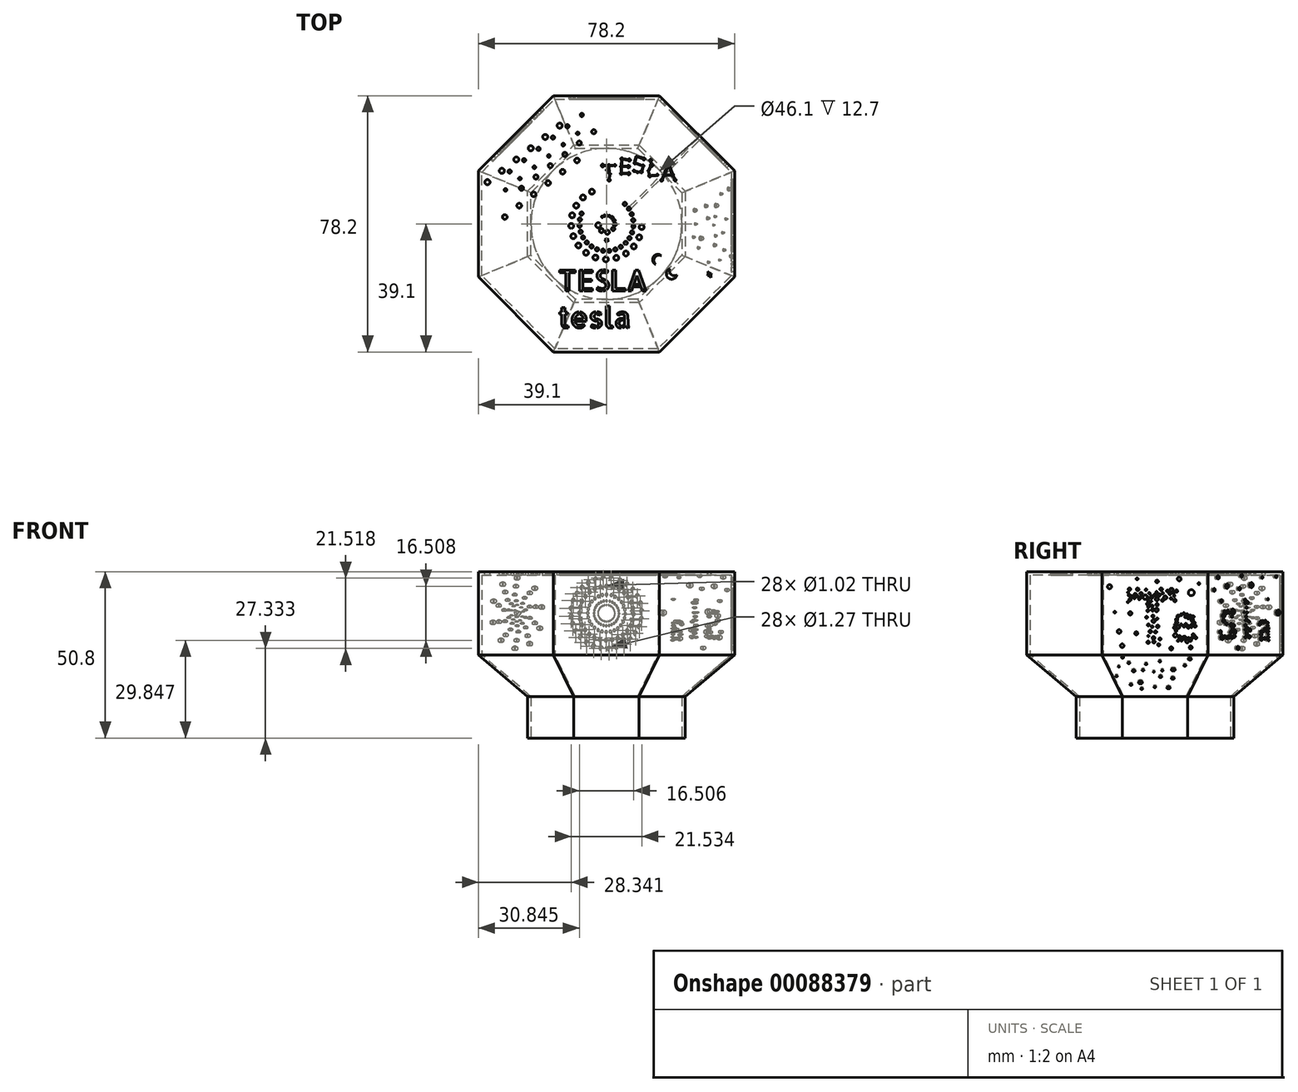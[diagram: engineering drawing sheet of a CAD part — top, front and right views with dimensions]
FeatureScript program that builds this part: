
annotation { "Feature Type Name" : "Feature", "Feature Type Description" : "" }
export const myFeature = defineFeature(function(context is Context, id is Id, definition is map)
    precondition{}
    {
        {
            var Q0;
            Q0=qCreatedBy(makeId("Top.planeOp"),FACE);
            cPlane(context, id + "F0", {"entities" : qUnion([Q0]), "cplaneType" : CPlaneType.OFFSET, "offset" : 12.7 * mm, "width" : 152.4 * mm, "height" : 152.4 * mm});
        }
        {
            var Q0;
            Q0=qCreatedBy(makeId("Top.planeOp"),FACE);
            cPlane(context, id + "F1", {"entities" : qUnion([Q0]), "cplaneType" : CPlaneType.OFFSET, "offset" : 25.4 * mm, "width" : 152.4 * mm, "height" : 152.4 * mm});
        }
        {
            var Q0;
            Q0=qCreatedBy(makeId("Top.planeOp"),FACE);
            cPlane(context, id + "F2", {"entities" : qUnion([Q0]), "cplaneType" : CPlaneType.OFFSET, "offset" : 50.8 * mm, "width" : 152.4 * mm, "height" : 152.4 * mm});
        }
        {
            var Q0;
            Q0=qCreatedBy(makeId("Top.planeOp"),FACE);
            var sketch = newSketch(context, id + "F3", { "sketchPlane" : qUnion([Q0])});
            skCircle(sketch, "E0", {"center": v(0, 0) * mm, "radius": 23.05 * mm});
            skCircle(sketch, "E1.cCircle", {"center": v(0, 0) * mm, "radius": 24.05 * mm, "construction": true});
            skLineSegment(sketch, "E1.0", {"start": v(-9.96, 24.05) * mm, "end": v(9.96, 24.05) * mm});
            skLineSegment(sketch, "E1.1", {"start": v(9.96, 24.05) * mm, "end": v(24.05, 9.96) * mm});
            skLineSegment(sketch, "E1.2", {"start": v(24.05, 9.96) * mm, "end": v(24.05, -9.96) * mm});
            skLineSegment(sketch, "E1.3", {"start": v(24.05, -9.96) * mm, "end": v(9.96, -24.05) * mm});
            skLineSegment(sketch, "E1.4", {"start": v(9.96, -24.05) * mm, "end": v(-9.96, -24.05) * mm});
            skLineSegment(sketch, "E1.5", {"start": v(-9.96, -24.05) * mm, "end": v(-24.05, -9.96) * mm});
            skLineSegment(sketch, "E1.6", {"start": v(-24.05, -9.96) * mm, "end": v(-24.05, 9.96) * mm});
            skLineSegment(sketch, "E1.7", {"start": v(-24.05, 9.96) * mm, "end": v(-9.96, 24.05) * mm});
            skPoint(sketch, "E1.0.midPoint", {"position": v(0, 24.05) * mm});
            skSolve(sketch);
        }
        {
            var Q0;
            Q0 = qSketchRegion(id + "F3", true);
            extrude(context, id + "F4", {"entities" : qUnion([Q0]), "depth" : 12.7 * mm});
        }
        {
            var Q0;
            Q0=qCreatedBy(id+"F1.planeOp",FACE);
            var sketch = newSketch(context, id + "F5", { "sketchPlane" : qUnion([Q0])});
            skCircle(sketch, "E2", {"center": v(0, 0) * mm, "radius": 38.1 * mm, "construction": true});
            skLineSegment(sketch, "E3.0", {"start": v(38.1, 15.78) * mm, "end": v(38.1, -15.78) * mm, "construction": true});
            skLineSegment(sketch, "E3.1", {"start": v(38.1, -15.78) * mm, "end": v(15.78, -38.1) * mm, "construction": true});
            skLineSegment(sketch, "E3.2", {"start": v(15.78, -38.1) * mm, "end": v(-15.78, -38.1) * mm, "construction": true});
            skLineSegment(sketch, "E3.3", {"start": v(-15.78, -38.1) * mm, "end": v(-38.1, -15.78) * mm, "construction": true});
            skLineSegment(sketch, "E3.4", {"start": v(-38.1, -15.78) * mm, "end": v(-38.1, 15.78) * mm, "construction": true});
            skLineSegment(sketch, "E3.5", {"start": v(-38.1, 15.78) * mm, "end": v(-15.78, 38.1) * mm, "construction": true});
            skLineSegment(sketch, "E3.6", {"start": v(-15.78, 38.1) * mm, "end": v(15.78, 38.1) * mm, "construction": true});
            skLineSegment(sketch, "E3.7", {"start": v(15.78, 38.1) * mm, "end": v(38.1, 15.78) * mm, "construction": true});
            skPoint(sketch, "E3.0.midPoint", {"position": v(38.1, 0) * mm});
            skCircle(sketch, "E4.cCircle", {"center": v(0, 0) * mm, "radius": 39.1 * mm, "construction": true});
            skLineSegment(sketch, "E4.0", {"start": v(-16.2, 39.1) * mm, "end": v(16.2, 39.1) * mm});
            skLineSegment(sketch, "E4.1", {"start": v(16.2, 39.1) * mm, "end": v(39.1, 16.2) * mm});
            skLineSegment(sketch, "E4.2", {"start": v(39.1, 16.2) * mm, "end": v(39.1, -16.2) * mm});
            skLineSegment(sketch, "E4.3", {"start": v(39.1, -16.2) * mm, "end": v(16.2, -39.1) * mm});
            skLineSegment(sketch, "E4.4", {"start": v(16.2, -39.1) * mm, "end": v(-16.2, -39.1) * mm});
            skLineSegment(sketch, "E4.5", {"start": v(-16.2, -39.1) * mm, "end": v(-39.1, -16.2) * mm});
            skLineSegment(sketch, "E4.6", {"start": v(-39.1, -16.2) * mm, "end": v(-39.1, 16.2) * mm});
            skLineSegment(sketch, "E4.7", {"start": v(-39.1, 16.2) * mm, "end": v(-16.2, 39.1) * mm});
            skPoint(sketch, "E4.0.midPoint", {"position": v(0, 39.1) * mm});
            skSolve(sketch);
        }
        {
            var Q0;
            Q0=makeQuery(id+"F4.opExtrude","CAP_FACE",FACE,{"disambiguationData":[OSD([sQuery(id+"F3.wireOp",EDGE,"E0"),sQuery(id+"F3.wireOp",EDGE,"E1.0"),sQuery(id+"F3.wireOp",EDGE,"E1.1"),sQuery(id+"F3.wireOp",EDGE,"E1.2"),sQuery(id+"F3.wireOp",EDGE,"E1.3"),sQuery(id+"F3.wireOp",EDGE,"E1.4"),sQuery(id+"F3.wireOp",EDGE,"E1.5"),sQuery(id+"F3.wireOp",EDGE,"E1.6"),sQuery(id+"F3.wireOp",EDGE,"E1.7")])],"isStart":false});
            var sketch = newSketch(context, id + "F6", { "sketchPlane" : qUnion([Q0])});
            skCircle(sketch, "E5.cCircle", {"center": v(0, 0) * mm, "radius": 24.05 * mm, "construction": true});
            skLineSegment(sketch, "E5.0", {"start": v(-9.96, 24.05) * mm, "end": v(9.96, 24.05) * mm});
            skLineSegment(sketch, "E5.1", {"start": v(9.96, 24.05) * mm, "end": v(24.05, 9.96) * mm});
            skLineSegment(sketch, "E5.2", {"start": v(24.05, 9.96) * mm, "end": v(24.05, -9.96) * mm});
            skLineSegment(sketch, "E5.3", {"start": v(24.05, -9.96) * mm, "end": v(9.96, -24.05) * mm});
            skLineSegment(sketch, "E5.4", {"start": v(9.96, -24.05) * mm, "end": v(-9.96, -24.05) * mm});
            skLineSegment(sketch, "E5.5", {"start": v(-9.96, -24.05) * mm, "end": v(-24.05, -9.96) * mm});
            skLineSegment(sketch, "E5.6", {"start": v(-24.05, -9.96) * mm, "end": v(-24.05, 9.96) * mm});
            skLineSegment(sketch, "E5.7", {"start": v(-24.05, 9.96) * mm, "end": v(-9.96, 24.05) * mm});
            skPoint(sketch, "E5.0.midPoint", {"position": v(0, 24.05) * mm});
            skCircle(sketch, "E6.cCircle", {"center": v(0, 0) * mm, "radius": 23.05 * mm, "construction": true});
            skLineSegment(sketch, "E6.0", {"start": v(-9.55, 23.05) * mm, "end": v(9.55, 23.05) * mm, "construction": true});
            skLineSegment(sketch, "E6.1", {"start": v(9.55, 23.05) * mm, "end": v(23.05, 9.55) * mm, "construction": true});
            skLineSegment(sketch, "E6.2", {"start": v(23.05, 9.55) * mm, "end": v(23.05, -9.55) * mm, "construction": true});
            skLineSegment(sketch, "E6.3", {"start": v(23.05, -9.55) * mm, "end": v(9.55, -23.05) * mm, "construction": true});
            skLineSegment(sketch, "E6.4", {"start": v(9.55, -23.05) * mm, "end": v(-9.55, -23.05) * mm, "construction": true});
            skLineSegment(sketch, "E6.5", {"start": v(-9.55, -23.05) * mm, "end": v(-23.05, -9.55) * mm, "construction": true});
            skLineSegment(sketch, "E6.6", {"start": v(-23.05, -9.55) * mm, "end": v(-23.05, 9.55) * mm, "construction": true});
            skLineSegment(sketch, "E6.7", {"start": v(-23.05, 9.55) * mm, "end": v(-9.55, 23.05) * mm, "construction": true});
            skPoint(sketch, "E6.0.midPoint", {"position": v(0, 23.05) * mm});
            skSolve(sketch);
        }
        {
            var Q1;
            Q1 = qSketchRegion(id + "F5", true);
            var Q2;
            Q2 = qSketchRegion(id + "F6", true);
            loft(context, id + "F7", {"operationType" : NewBodyOperationType.ADD, "sheetProfilesArray" : [{ "sheetProfileEntities" : qUnion([Q1]) }, { "sheetProfileEntities" : qUnion([Q2]) }]});
        }
        {
            var Q0;
            Q0=qCreatedBy(id+"F0.planeOp",FACE);
            var sketch = newSketch(context, id + "F8", { "sketchPlane" : qUnion([Q0])});
            skCircle(sketch, "E7.cCircle", {"center": v(0, 0) * mm, "radius": 23.05 * mm, "construction": true});
            skLineSegment(sketch, "E7.0", {"start": v(-9.55, 23.05) * mm, "end": v(9.55, 23.05) * mm});
            skLineSegment(sketch, "E7.1", {"start": v(9.55, 23.05) * mm, "end": v(23.05, 9.55) * mm});
            skLineSegment(sketch, "E7.2", {"start": v(23.05, 9.55) * mm, "end": v(23.05, -9.55) * mm});
            skLineSegment(sketch, "E7.3", {"start": v(23.05, -9.55) * mm, "end": v(9.55, -23.05) * mm});
            skLineSegment(sketch, "E7.4", {"start": v(9.55, -23.05) * mm, "end": v(-9.55, -23.05) * mm});
            skLineSegment(sketch, "E7.5", {"start": v(-9.55, -23.05) * mm, "end": v(-23.05, -9.55) * mm});
            skLineSegment(sketch, "E7.6", {"start": v(-23.05, -9.55) * mm, "end": v(-23.05, 9.55) * mm});
            skLineSegment(sketch, "E7.7", {"start": v(-23.05, 9.55) * mm, "end": v(-9.55, 23.05) * mm});
            skPoint(sketch, "E7.0.midPoint", {"position": v(0, 23.05) * mm});
            skSolve(sketch);
        }
        {
            var Q0;
            Q0=qCreatedBy(id+"F1.planeOp",FACE);
            var sketch = newSketch(context, id + "F9", { "sketchPlane" : qUnion([Q0])});
            skCircle(sketch, "E8.cCircle", {"center": v(0, 0) * mm, "radius": 38.1 * mm, "construction": true});
            skLineSegment(sketch, "E8.0", {"start": v(-15.78, 38.1) * mm, "end": v(15.78, 38.1) * mm});
            skLineSegment(sketch, "E8.1", {"start": v(15.78, 38.1) * mm, "end": v(38.1, 15.78) * mm});
            skLineSegment(sketch, "E8.2", {"start": v(38.1, 15.78) * mm, "end": v(38.1, -15.78) * mm});
            skLineSegment(sketch, "E8.3", {"start": v(38.1, -15.78) * mm, "end": v(15.78, -38.1) * mm});
            skLineSegment(sketch, "E8.4", {"start": v(15.78, -38.1) * mm, "end": v(-15.78, -38.1) * mm});
            skLineSegment(sketch, "E8.5", {"start": v(-15.78, -38.1) * mm, "end": v(-38.1, -15.78) * mm});
            skLineSegment(sketch, "E8.6", {"start": v(-38.1, -15.78) * mm, "end": v(-38.1, 15.78) * mm});
            skLineSegment(sketch, "E8.7", {"start": v(-38.1, 15.78) * mm, "end": v(-15.78, 38.1) * mm});
            skPoint(sketch, "E8.0.midPoint", {"position": v(0, 38.1) * mm});
            skSolve(sketch);
        }
        {
            var Q1;
            Q1 = qSketchRegion(id + "F8", true);
            var Q2;
            Q2 = qSketchRegion(id + "F9", true);
            loft(context, id + "F10", {"operationType" : NewBodyOperationType.REMOVE, "sheetProfilesArray" : [{ "sheetProfileEntities" : qUnion([Q1]) }, { "sheetProfileEntities" : qUnion([Q2]) }]});
        }
        {
            var Q0;
            Q0=qCreatedBy(id+"F1.planeOp",FACE);
            var sketch = newSketch(context, id + "F11", { "sketchPlane" : qUnion([Q0])});
            skCircle(sketch, "E9.cCircle", {"center": v(0, 0) * mm, "radius": 39.1 * mm, "construction": true});
            skLineSegment(sketch, "E9.0", {"start": v(-16.2, 39.1) * mm, "end": v(16.2, 39.1) * mm});
            skLineSegment(sketch, "E9.1", {"start": v(16.2, 39.1) * mm, "end": v(39.1, 16.2) * mm});
            skLineSegment(sketch, "E9.2", {"start": v(39.1, 16.2) * mm, "end": v(39.1, -16.2) * mm});
            skLineSegment(sketch, "E9.3", {"start": v(39.1, -16.2) * mm, "end": v(16.2, -39.1) * mm});
            skLineSegment(sketch, "E9.4", {"start": v(16.2, -39.1) * mm, "end": v(-16.2, -39.1) * mm});
            skLineSegment(sketch, "E9.5", {"start": v(-16.2, -39.1) * mm, "end": v(-39.1, -16.2) * mm});
            skLineSegment(sketch, "E9.6", {"start": v(-39.1, -16.2) * mm, "end": v(-39.1, 16.2) * mm});
            skLineSegment(sketch, "E9.7", {"start": v(-39.1, 16.2) * mm, "end": v(-16.2, 39.1) * mm});
            skPoint(sketch, "E9.0.midPoint", {"position": v(0, 39.1) * mm});
            skSolve(sketch);
        }
        {
            var Q0;
            Q0=qCreatedBy(id+"F2.planeOp",FACE);
            var sketch = newSketch(context, id + "F12", { "sketchPlane" : qUnion([Q0])});
            skCircle(sketch, "E10.cCircle", {"center": v(0, 0) * mm, "radius": 39.1 * mm, "construction": true});
            skLineSegment(sketch, "E10.0", {"start": v(-16.2, 39.1) * mm, "end": v(16.2, 39.1) * mm});
            skLineSegment(sketch, "E10.1", {"start": v(16.2, 39.1) * mm, "end": v(39.1, 16.2) * mm});
            skLineSegment(sketch, "E10.2", {"start": v(39.1, 16.2) * mm, "end": v(39.1, -16.2) * mm});
            skLineSegment(sketch, "E10.3", {"start": v(39.1, -16.2) * mm, "end": v(16.2, -39.1) * mm});
            skLineSegment(sketch, "E10.4", {"start": v(16.2, -39.1) * mm, "end": v(-16.2, -39.1) * mm});
            skLineSegment(sketch, "E10.5", {"start": v(-16.2, -39.1) * mm, "end": v(-39.1, -16.2) * mm});
            skLineSegment(sketch, "E10.6", {"start": v(-39.1, -16.2) * mm, "end": v(-39.1, 16.2) * mm});
            skLineSegment(sketch, "E10.7", {"start": v(-39.1, 16.2) * mm, "end": v(-16.2, 39.1) * mm});
            skPoint(sketch, "E10.0.midPoint", {"position": v(0, 39.1) * mm});
            skSolve(sketch);
        }
        {
            var Q1;
            Q1 = qSketchRegion(id + "F11", true);
            var Q2;
            Q2 = qSketchRegion(id + "F12", true);
            loft(context, id + "F13", {"operationType" : NewBodyOperationType.ADD, "sheetProfilesArray" : [{ "sheetProfileEntities" : qUnion([Q1]) }, { "sheetProfileEntities" : qUnion([Q2]) }]});
        }
        {
            var Q0;
            Q0=qCreatedBy(id+"F1.planeOp",FACE);
            var sketch = newSketch(context, id + "F14", { "sketchPlane" : qUnion([Q0])});
            skCircle(sketch, "E11.cCircle", {"center": v(0, 0) * mm, "radius": 38.1 * mm, "construction": true});
            skLineSegment(sketch, "E11.0", {"start": v(-15.78, 38.1) * mm, "end": v(15.78, 38.1) * mm});
            skLineSegment(sketch, "E11.1", {"start": v(15.78, 38.1) * mm, "end": v(38.1, 15.78) * mm});
            skLineSegment(sketch, "E11.2", {"start": v(38.1, 15.78) * mm, "end": v(38.1, -15.78) * mm});
            skLineSegment(sketch, "E11.3", {"start": v(38.1, -15.78) * mm, "end": v(15.78, -38.1) * mm});
            skLineSegment(sketch, "E11.4", {"start": v(15.78, -38.1) * mm, "end": v(-15.78, -38.1) * mm});
            skLineSegment(sketch, "E11.5", {"start": v(-15.78, -38.1) * mm, "end": v(-38.1, -15.78) * mm});
            skLineSegment(sketch, "E11.6", {"start": v(-38.1, -15.78) * mm, "end": v(-38.1, 15.78) * mm});
            skLineSegment(sketch, "E11.7", {"start": v(-38.1, 15.78) * mm, "end": v(-15.78, 38.1) * mm});
            skPoint(sketch, "E11.0.midPoint", {"position": v(0, 38.1) * mm});
            skSolve(sketch);
        }
        {
            var Q0;
            Q0 = qSketchRegion(id + "F14", true);
            var Q1;
            Q1=makeQuery(id+"F13.opLoft","CAP_FACE",FACE,{"disambiguationData":[OSD([makeQuery(id+"F12.imprint","IMPRINT",FACE,{"disambiguationData":[TD([[makeQuery(id+"F12.imprint","IMPRINT",EDGE,{"derivedFrom":sQuery(id+"F12.wireOp",EDGE,"E10.0")}),-1.0]])]})])],"isStart":true});
            extrude(context, id + "F15", {"entities" : qUnion([Q0]), "operationType" : NewBodyOperationType.REMOVE, "endBoundEntityFace" : qUnion([Q1]), "depth" : 25.4 * mm - 1 * mm});
        }
        {
            var Q0;
            Q0=makeQuery(id+"F13.opLoft","CAP_FACE",FACE,{"disambiguationData":[OSD([makeQuery(id+"F12.imprint","IMPRINT",FACE,{"disambiguationData":[TD([[makeQuery(id+"F12.imprint","IMPRINT",EDGE,{"derivedFrom":sQuery(id+"F12.wireOp",EDGE,"E10.0")}),-1.0]])]})])],"isStart":true});
            var sketch = newSketch(context, id + "F16", { "sketchPlane" : qUnion([Q0])});
            skCircle(sketch, "E12", {"center": v(0, 0) * mm, "radius": 2.54 * mm, "construction": true});
            skCircle(sketch, "E13", {"center": v(1.72, 1.87) * mm, "radius": 0.38 * mm});
            skCircle(sketch, "E14", {"center": v(2.54, -0.12) * mm, "radius": 0.5 * mm});
            skCircle(sketch, "E15", {"center": v(-2.5, -0.4) * mm, "radius": 0.76 * mm});
            skCircle(sketch, "E16", {"center": v(0.28, -2.52) * mm, "radius": 0.64 * mm});
            skCircle(sketch, "E17", {"center": v(0.16, 2.53) * mm, "radius": 0.25 * mm});
            skCircle(sketch, "E18", {"center": v(-1.3, 2.18) * mm, "radius": 0.25 * mm});
            skCircle(sketch, "E19", {"center": v(-0.6, 2.47) * mm, "radius": 0.25 * mm});
            skCircle(sketch, "E20", {"center": v(0.93, 2.37) * mm, "radius": 0.25 * mm});
            skCircle(sketch, "E21", {"center": v(2.32, 1.03) * mm, "radius": 0.38 * mm});
            skCircle(sketch, "E22", {"center": v(-1.55, -2.01) * mm, "radius": 0.64 * mm});
            skLineSegment(sketch, "E23", {"start": v(-0.08, -4.77) * mm, "end": v(0.16, -4.32) * mm});
            skLineSegment(sketch, "E24", {"start": v(0.16, -4.32) * mm, "end": v(0.25, -4.82) * mm});
            skLineSegment(sketch, "E25", {"start": v(0.25, -4.82) * mm, "end": v(0.75, -4.82) * mm});
            skLineSegment(sketch, "E26", {"start": v(0.75, -4.82) * mm, "end": v(0.32, -5.08) * mm});
            skLineSegment(sketch, "E27", {"start": v(0.32, -5.08) * mm, "end": v(0.4, -5.58) * mm});
            skLineSegment(sketch, "E28", {"start": v(0.4, -5.58) * mm, "end": v(0, -5.27) * mm});
            skLineSegment(sketch, "E29", {"start": v(0, -5.27) * mm, "end": v(-0.44, -5.52) * mm});
            skLineSegment(sketch, "E30", {"start": v(-0.44, -5.52) * mm, "end": v(-0.2, -5.08) * mm});
            skLineSegment(sketch, "E31", {"start": v(-0.2, -5.08) * mm, "end": v(-0.6, -4.77) * mm});
            skLineSegment(sketch, "E32", {"start": v(-0.6, -4.77) * mm, "end": v(-0.08, -4.77) * mm});
            skCircle(sketch, "E33", {"center": v(0, 0) * mm, "radius": 8.26 * mm, "construction": true});
            skCircle(sketch, "E34", {"center": v(5.59, 6.08) * mm, "radius": 0.5 * mm});
            skCircle(sketch, "E35.1.0", {"center": v(6.82, 4.65) * mm, "radius": 0.5 * mm});
            skCircle(sketch, "E35.2.0", {"center": v(7.7, 2.97) * mm, "radius": 0.5 * mm});
            skCircle(sketch, "E35.3.0", {"center": v(8.18, 1.14) * mm, "radius": 0.5 * mm});
            skCircle(sketch, "E35.4.0", {"center": v(8.22, -0.75) * mm, "radius": 0.5 * mm});
            skCircle(sketch, "E35.5.0", {"center": v(7.83, -2.6) * mm, "radius": 0.5 * mm});
            skCircle(sketch, "E35.6.0", {"center": v(7.04, -4.32) * mm, "radius": 0.5 * mm});
            skCircle(sketch, "E35.7.0", {"center": v(5.87, -5.8) * mm, "radius": 0.5 * mm});
            skCircle(sketch, "E35.8.0", {"center": v(4.4, -6.99) * mm, "radius": 0.5 * mm});
            skCircle(sketch, "E35.9.0", {"center": v(2.69, -7.8) * mm, "radius": 0.5 * mm});
            skCircle(sketch, "E35.10.0", {"center": v(0.84, -8.21) * mm, "radius": 0.5 * mm});
            skCircle(sketch, "E35.11.0", {"center": v(-1.05, -8.19) * mm, "radius": 0.5 * mm});
            skCircle(sketch, "E35.12.0", {"center": v(-2.89, -7.73) * mm, "radius": 0.5 * mm});
            skCircle(sketch, "E35.13.0", {"center": v(-4.57, -6.87) * mm, "radius": 0.5 * mm});
            skCircle(sketch, "E35.14.0", {"center": v(-6.02, -5.65) * mm, "radius": 0.5 * mm});
            skCircle(sketch, "E35.15.0", {"center": v(-7.15, -4.13) * mm, "radius": 0.5 * mm});
            skCircle(sketch, "E35.16.0", {"center": v(-7.9, -2.4) * mm, "radius": 0.5 * mm});
            skCircle(sketch, "E35.17.0", {"center": v(-8.24, -0.54) * mm, "radius": 0.5 * mm});
            skCircle(sketch, "E35.18.0", {"center": v(-8.14, 1.35) * mm, "radius": 0.5 * mm});
            skCircle(sketch, "E35.19.0", {"center": v(-7.62, 3.17) * mm, "radius": 0.5 * mm});
            skLineSegment(sketch, "E35.anchor1", {"start": v(0, 0) * mm, "end": v(5.59, 6.08) * mm, "construction": true});
            skLineSegment(sketch, "E35.anchor2", {"start": v(0, 0) * mm, "end": v(-7.62, 3.17) * mm, "construction": true});
            skCircle(sketch, "E36", {"center": v(-1.15, 17.81) * mm, "radius": 0.42 * mm});
            skCircle(sketch, "E37", {"center": v(0.73, 17.81) * mm, "radius": 0.32 * mm});
            skCircle(sketch, "E38", {"center": v(2.59, 17.9) * mm, "radius": 0.28 * mm});
            skCircle(sketch, "E39", {"center": v(0.03, 16.44) * mm, "radius": 0.17 * mm});
            skCircle(sketch, "E40", {"center": v(1.07, 15.26) * mm, "radius": 0.23 * mm});
            skCircle(sketch, "E41", {"center": v(0.8, 13.4) * mm, "radius": 0.36 * mm});
            skCircle(sketch, "E42", {"center": v(4.53, 15.37) * mm, "radius": 0.32 * mm});
            skCircle(sketch, "E43", {"center": v(6.8, 15.37) * mm, "radius": 0.38 * mm});
            skCircle(sketch, "E44", {"center": v(4.55, 17.54) * mm, "radius": 0.3 * mm});
            skCircle(sketch, "E45", {"center": v(6.72, 17.5) * mm, "radius": 0.4 * mm});
            skCircle(sketch, "E46", {"center": v(4.71, 19.86) * mm, "radius": 0.34 * mm});
            skCircle(sketch, "E47", {"center": v(6.97, 19.5) * mm, "radius": 0.37 * mm});
            skCircle(sketch, "E48", {"center": v(11.42, 19.86) * mm, "radius": 0.36 * mm});
            skCircle(sketch, "E49", {"center": v(9.15, 20.43) * mm, "radius": 0.22 * mm});
            skCircle(sketch, "E50", {"center": v(8.7, 18.6) * mm, "radius": 0.3 * mm});
            skCircle(sketch, "E51", {"center": v(11.17, 17.73) * mm, "radius": 0.3 * mm});
            skCircle(sketch, "E52", {"center": v(10.66, 15.92) * mm, "radius": 0.36 * mm});
            skCircle(sketch, "E53", {"center": v(9.46, 15.77) * mm, "radius": 0.21 * mm});
            skCircle(sketch, "E54", {"center": v(8.36, 16.23) * mm, "radius": 0.22 * mm});
            skCircle(sketch, "E55", {"center": v(13.5, 19.44) * mm, "radius": 0.34 * mm});
            skCircle(sketch, "E56", {"center": v(13.78, 17.9) * mm, "radius": 0.42 * mm});
            skCircle(sketch, "E57", {"center": v(12.83, 16.23) * mm, "radius": 0.2 * mm});
            skCircle(sketch, "E58", {"center": v(13.23, 14.65) * mm, "radius": 0.34 * mm});
            skCircle(sketch, "E59", {"center": v(15.55, 14.95) * mm, "radius": 0.24 * mm});
            skCircle(sketch, "E60", {"center": v(16.82, 13.32) * mm, "radius": 0.32 * mm});
            skCircle(sketch, "E61", {"center": v(17.66, 14.93) * mm, "radius": 0.3 * mm});
            skCircle(sketch, "E62", {"center": v(19.11, 17.65) * mm, "radius": 0.38 * mm});
            skCircle(sketch, "E63", {"center": v(20.15, 14.99) * mm, "radius": 0.36 * mm});
            skCircle(sketch, "E64", {"center": v(20.97, 13.4) * mm, "radius": 0.32 * mm});
            skLineSegment(sketch, "E65.bottom", {"start": v(-0.51, 17.9) * mm, "end": v(0.2, 17.9) * mm});
            skLineSegment(sketch, "E65.top", {"start": v(-0.51, 17.75) * mm, "end": v(0.2, 17.75) * mm});
            skLineSegment(sketch, "E65.left", {"start": v(-0.51, 17.9) * mm, "end": v(-0.51, 17.75) * mm});
            skLineSegment(sketch, "E65.right", {"start": v(0.2, 17.9) * mm, "end": v(0.2, 17.75) * mm});
            skLineSegment(sketch, "E66.bottom", {"start": v(1.28, 17.94) * mm, "end": v(2.1, 17.94) * mm});
            skLineSegment(sketch, "E66.top", {"start": v(1.28, 17.8) * mm, "end": v(2.1, 17.8) * mm});
            skLineSegment(sketch, "E66.left", {"start": v(1.28, 17.94) * mm, "end": v(1.28, 17.8) * mm});
            skLineSegment(sketch, "E66.right", {"start": v(2.1, 17.94) * mm, "end": v(2.1, 17.8) * mm});
            skLineSegment(sketch, "E67", {"start": v(0.7, 15.42) * mm, "end": v(0.77, 15.52) * mm});
            skLineSegment(sketch, "E68", {"start": v(0.77, 15.52) * mm, "end": v(0.2, 16.26) * mm});
            skLineSegment(sketch, "E69", {"start": v(0.92, 14.9) * mm, "end": v(0.78, 13.93) * mm});
            skLineSegment(sketch, "E70", {"start": v(0.78, 13.93) * mm, "end": v(0.91, 13.9) * mm});
            skLineSegment(sketch, "E71", {"start": v(0.91, 13.9) * mm, "end": v(1.05, 14.88) * mm});
            skLineSegment(sketch, "E72", {"start": v(1.05, 14.88) * mm, "end": v(0.92, 14.9) * mm});
            skLineSegment(sketch, "E73", {"start": v(0.9, 15.73) * mm, "end": v(0.98, 15.76) * mm});
            skLineSegment(sketch, "E74", {"start": v(0.98, 15.76) * mm, "end": v(0.8, 17.35) * mm});
            skLineSegment(sketch, "E75", {"start": v(0.43, 17.44) * mm, "end": v(0.18, 16.87) * mm});
            skLineSegment(sketch, "E76", {"start": v(0.18, 16.87) * mm, "end": v(0.3, 16.84) * mm});
            skLineSegment(sketch, "E77", {"start": v(0.3, 16.84) * mm, "end": v(0.52, 17.4) * mm});
            skLineSegment(sketch, "E78", {"start": v(0.52, 17.4) * mm, "end": v(0.43, 17.44) * mm});
            skLineSegment(sketch, "E79", {"start": v(5.24, 19.88) * mm, "end": v(6.44, 19.67) * mm});
            skLineSegment(sketch, "E80", {"start": v(6.44, 19.67) * mm, "end": v(6.41, 19.47) * mm});
            skLineSegment(sketch, "E81", {"start": v(6.41, 19.47) * mm, "end": v(5.2, 19.69) * mm});
            skLineSegment(sketch, "E82", {"start": v(5.24, 19.88) * mm, "end": v(5.2, 19.69) * mm});
            skLineSegment(sketch, "E83", {"start": v(4.54, 19.35) * mm, "end": v(4.45, 18.03) * mm});
            skLineSegment(sketch, "E84", {"start": v(4.45, 18.03) * mm, "end": v(4.67, 18) * mm});
            skLineSegment(sketch, "E85", {"start": v(4.67, 18) * mm, "end": v(4.72, 19.33) * mm});
            skLineSegment(sketch, "E86", {"start": v(4.72, 19.33) * mm, "end": v(4.54, 19.35) * mm});
            skLineSegment(sketch, "E87", {"start": v(5, 17.65) * mm, "end": v(5, 17.45) * mm});
            skLineSegment(sketch, "E88", {"start": v(5, 17.45) * mm, "end": v(6.18, 17.46) * mm});
            skLineSegment(sketch, "E89", {"start": v(6.18, 17.46) * mm, "end": v(6.19, 17.65) * mm});
            skLineSegment(sketch, "E90", {"start": v(6.19, 17.65) * mm, "end": v(5, 17.65) * mm});
            skLineSegment(sketch, "E91", {"start": v(4.5, 17.09) * mm, "end": v(4.5, 15.9) * mm});
            skLineSegment(sketch, "E92", {"start": v(4.5, 15.9) * mm, "end": v(4.65, 15.86) * mm});
            skLineSegment(sketch, "E93", {"start": v(4.65, 15.86) * mm, "end": v(4.65, 17.09) * mm});
            skLineSegment(sketch, "E94", {"start": v(4.65, 17.09) * mm, "end": v(4.5, 17.09) * mm});
            skLineSegment(sketch, "E95", {"start": v(4.99, 15.5) * mm, "end": v(4.99, 15.3) * mm});
            skLineSegment(sketch, "E96", {"start": v(4.99, 15.3) * mm, "end": v(6.28, 15.29) * mm});
            skLineSegment(sketch, "E97", {"start": v(6.28, 15.29) * mm, "end": v(6.32, 15.5) * mm});
            skLineSegment(sketch, "E98", {"start": v(6.32, 15.5) * mm, "end": v(4.99, 15.5) * mm});
            skLineSegment(sketch, "E99", {"start": v(9.12, 15.83) * mm, "end": v(9.17, 15.94) * mm});
            skLineSegment(sketch, "E100", {"start": v(9.17, 15.94) * mm, "end": v(8.68, 16.17) * mm});
            skLineSegment(sketch, "E101", {"start": v(8.64, 16.04) * mm, "end": v(8.68, 16.17) * mm});
            skLineSegment(sketch, "E102", {"start": v(9.76, 15.84) * mm, "end": v(9.76, 15.7) * mm});
            skLineSegment(sketch, "E103", {"start": v(9.76, 15.7) * mm, "end": v(10.23, 15.8) * mm});
            skLineSegment(sketch, "E104", {"start": v(10.23, 15.8) * mm, "end": v(10.15, 15.93) * mm});
            skLineSegment(sketch, "E105", {"start": v(10.15, 15.93) * mm, "end": v(9.76, 15.84) * mm});
            skLineSegment(sketch, "E106", {"start": v(10.8, 16.37) * mm, "end": v(11.04, 17.35) * mm});
            skLineSegment(sketch, "E107", {"start": v(11.04, 17.35) * mm, "end": v(11.14, 17.33) * mm});
            skLineSegment(sketch, "E108", {"start": v(11.14, 17.33) * mm, "end": v(10.9, 16.34) * mm});
            skLineSegment(sketch, "E109", {"start": v(10.9, 16.34) * mm, "end": v(10.8, 16.37) * mm});
            skLineSegment(sketch, "E110", {"start": v(10.84, 17.94) * mm, "end": v(9.15, 18.5) * mm});
            skLineSegment(sketch, "E111", {"start": v(9.15, 18.5) * mm, "end": v(9.08, 18.4) * mm});
            skLineSegment(sketch, "E112", {"start": v(9.08, 18.4) * mm, "end": v(10.77, 17.82) * mm});
            skLineSegment(sketch, "E113", {"start": v(10.77, 17.82) * mm, "end": v(10.84, 17.94) * mm});
            skLineSegment(sketch, "E114", {"start": v(8.9, 20.17) * mm, "end": v(8.59, 19.04) * mm});
            skLineSegment(sketch, "E115", {"start": v(8.59, 19.04) * mm, "end": v(8.75, 19.02) * mm});
            skLineSegment(sketch, "E116", {"start": v(8.75, 19.02) * mm, "end": v(9.02, 20.1) * mm});
            skLineSegment(sketch, "E117", {"start": v(9.02, 20.1) * mm, "end": v(8.9, 20.17) * mm});
            skLineSegment(sketch, "E118", {"start": v(9.58, 20.55) * mm, "end": v(11.03, 20.18) * mm});
            skLineSegment(sketch, "E119", {"start": v(11.03, 20.18) * mm, "end": v(10.93, 19.98) * mm});
            skLineSegment(sketch, "E120", {"start": v(10.93, 19.98) * mm, "end": v(9.5, 20.4) * mm});
            skLineSegment(sketch, "E121", {"start": v(9.5, 20.4) * mm, "end": v(9.58, 20.55) * mm});
            skLineSegment(sketch, "E122", {"start": v(13.46, 19) * mm, "end": v(13.56, 18.45) * mm});
            skLineSegment(sketch, "E123", {"start": v(13.56, 18.45) * mm, "end": v(13.7, 18.48) * mm});
            skLineSegment(sketch, "E124", {"start": v(13.7, 18.48) * mm, "end": v(13.58, 19) * mm});
            skLineSegment(sketch, "E125", {"start": v(13.58, 19) * mm, "end": v(13.46, 19) * mm});
            skLineSegment(sketch, "E126", {"start": v(13.3, 17.54) * mm, "end": v(12.98, 16.6) * mm});
            skLineSegment(sketch, "E127", {"start": v(12.98, 16.6) * mm, "end": v(13.11, 16.5) * mm});
            skLineSegment(sketch, "E128", {"start": v(13.11, 16.5) * mm, "end": v(13.44, 17.45) * mm});
            skLineSegment(sketch, "E129", {"start": v(13.44, 17.45) * mm, "end": v(13.3, 17.54) * mm});
            skLineSegment(sketch, "E130", {"start": v(12.8, 15.83) * mm, "end": v(12.92, 15.11) * mm});
            skLineSegment(sketch, "E131", {"start": v(12.92, 15.11) * mm, "end": v(13.05, 15.2) * mm});
            skLineSegment(sketch, "E132", {"start": v(13.05, 15.2) * mm, "end": v(12.91, 15.85) * mm});
            skLineSegment(sketch, "E133", {"start": v(12.91, 15.85) * mm, "end": v(12.8, 15.83) * mm});
            skLineSegment(sketch, "E134", {"start": v(13.68, 14.83) * mm, "end": v(15.14, 14.95) * mm});
            skLineSegment(sketch, "E135", {"start": v(15.14, 14.95) * mm, "end": v(15.15, 14.72) * mm});
            skLineSegment(sketch, "E136", {"start": v(15.15, 14.72) * mm, "end": v(13.7, 14.6) * mm});
            skLineSegment(sketch, "E137", {"start": v(13.7, 14.6) * mm, "end": v(13.68, 14.83) * mm});
            skLineSegment(sketch, "E138", {"start": v(17, 13.77) * mm, "end": v(17.3, 14.6) * mm});
            skLineSegment(sketch, "E139", {"start": v(17.3, 14.6) * mm, "end": v(17.49, 14.51) * mm});
            skLineSegment(sketch, "E140", {"start": v(17.49, 14.51) * mm, "end": v(17.19, 13.7) * mm});
            skLineSegment(sketch, "E141", {"start": v(17.19, 13.7) * mm, "end": v(17, 13.77) * mm});
            skLineSegment(sketch, "E142", {"start": v(18.14, 14.97) * mm, "end": v(19.61, 14.97) * mm});
            skLineSegment(sketch, "E143", {"start": v(19.61, 14.97) * mm, "end": v(19.66, 14.8) * mm});
            skLineSegment(sketch, "E144", {"start": v(19.66, 14.8) * mm, "end": v(18.13, 14.78) * mm});
            skLineSegment(sketch, "E145", {"start": v(18.13, 14.78) * mm, "end": v(18.14, 14.97) * mm});
            skLineSegment(sketch, "E146", {"start": v(18.57, 17.47) * mm, "end": v(17.74, 15.57) * mm});
            skLineSegment(sketch, "E147", {"start": v(17.74, 15.57) * mm, "end": v(17.94, 15.47) * mm});
            skLineSegment(sketch, "E148", {"start": v(17.94, 15.47) * mm, "end": v(18.66, 17.3) * mm});
            skLineSegment(sketch, "E149", {"start": v(18.66, 17.3) * mm, "end": v(18.57, 17.47) * mm});
            skLineSegment(sketch, "E150", {"start": v(19.27, 17.18) * mm, "end": v(19.41, 17.24) * mm});
            skLineSegment(sketch, "E151", {"start": v(19.41, 17.24) * mm, "end": v(20.06, 15.54) * mm});
            skLineSegment(sketch, "E152", {"start": v(20.06, 15.54) * mm, "end": v(19.85, 15.44) * mm});
            skLineSegment(sketch, "E153", {"start": v(19.85, 15.44) * mm, "end": v(19.27, 17.18) * mm});
            skLineSegment(sketch, "E154", {"start": v(20.31, 14.53) * mm, "end": v(20.67, 13.77) * mm});
            skLineSegment(sketch, "E155", {"start": v(20.67, 13.77) * mm, "end": v(20.8, 13.82) * mm});
            skLineSegment(sketch, "E156", {"start": v(20.8, 13.82) * mm, "end": v(20.49, 14.56) * mm});
            skLineSegment(sketch, "E157", {"start": v(20.49, 14.56) * mm, "end": v(20.31, 14.53) * mm});
            skCircle(sketch, "E158", {"center": v(0, 0) * mm, "radius": 10.8 * mm, "construction": true});
            skCircle(sketch, "E159", {"center": v(10.75, -0.97) * mm, "radius": 0.76 * mm});
            skCircle(sketch, "E160.1.0", {"center": v(9.99, -4.1) * mm, "radius": 0.76 * mm});
            skCircle(sketch, "E160.2.0", {"center": v(8.33, -6.86) * mm, "radius": 0.76 * mm});
            skCircle(sketch, "E160.3.0", {"center": v(5.94, -9.02) * mm, "radius": 0.76 * mm});
            skCircle(sketch, "E160.4.0", {"center": v(3, -10.37) * mm, "radius": 0.76 * mm});
            skCircle(sketch, "E160.5.0", {"center": v(-0.19, -10.8) * mm, "radius": 0.76 * mm});
            skCircle(sketch, "E160.6.0", {"center": v(-3.36, -10.26) * mm, "radius": 0.76 * mm});
            skCircle(sketch, "E160.7.0", {"center": v(-6.24, -8.8) * mm, "radius": 0.76 * mm});
            skCircle(sketch, "E160.8.0", {"center": v(-8.56, -6.57) * mm, "radius": 0.76 * mm});
            skCircle(sketch, "E160.9.0", {"center": v(-10.12, -3.75) * mm, "radius": 0.76 * mm});
            skCircle(sketch, "E160.10.0", {"center": v(-10.78, -0.6) * mm, "radius": 0.76 * mm});
            skCircle(sketch, "E160.11.0", {"center": v(-10.47, 2.61) * mm, "radius": 0.76 * mm});
            skCircle(sketch, "E160.12.0", {"center": v(-9.24, 5.59) * mm, "radius": 0.76 * mm});
            skCircle(sketch, "E160.13.0", {"center": v(-7.17, 8.07) * mm, "radius": 0.76 * mm});
            skCircle(sketch, "E160.14.0", {"center": v(-4.47, 9.82) * mm, "radius": 0.76 * mm});
            skLineSegment(sketch, "E160.anchor1", {"start": v(0, 0) * mm, "end": v(10.75, -0.97) * mm, "construction": true});
            skLineSegment(sketch, "E160.anchor2", {"start": v(0, 0) * mm, "end": v(-4.47, 9.82) * mm, "construction": true});
            skArc(sketch, "E161", {"start": v(19.31, -13.7) * mm, "mid": v(19.74, -15.41) * mm, "end": v(21.49, -15.65) * mm});
            skArc(sketch, "E162", {"start": v(19.31, -13.7) * mm, "mid": v(18.8, -16.45) * mm, "end": v(21.49, -15.65) * mm});
            skArc(sketch, "E163", {"start": v(16.75, -9.7) * mm, "mid": v(14.71, -10.24) * mm, "end": v(14.98, -12.34) * mm});
            skArc(sketch, "E164", {"start": v(16.75, -9.7) * mm, "mid": v(14.35, -10) * mm, "end": v(14.98, -12.34) * mm});
            skArc(sketch, "E165", {"start": v(30.87, -15.73) * mm, "mid": v(31.02, -15.15) * mm, "end": v(31, -14.54) * mm});
            skArc(sketch, "E166", {"start": v(31, -14.54) * mm, "mid": v(31.45, -14.94) * mm, "end": v(32, -15.17) * mm});
            skArc(sketch, "E167", {"start": v(31.89, -16.36) * mm, "mid": v(31.43, -15.97) * mm, "end": v(30.87, -15.73) * mm});
            skArc(sketch, "E168", {"start": v(32, -15.17) * mm, "mid": v(31.86, -15.76) * mm, "end": v(31.89, -16.36) * mm});
            skLineSegment(sketch, "E169", {"start": v(29.07, -14.95) * mm, "end": v(30.4, -17.64) * mm, "construction": true});
            skLineSegment(sketch, "E170", {"start": v(32.49, -13.27) * mm, "end": v(33.81, -15.96) * mm, "construction": true});
            skLineSegment(sketch, "E171", {"start": v(29.07, -14.95) * mm, "end": v(32.49, -13.27) * mm, "construction": true});
            skLineSegment(sketch, "E172", {"start": v(30.4, -17.64) * mm, "end": v(33.81, -15.96) * mm, "construction": true});
            skLineSegment(sketch, "E173", {"start": v(30.87, -15.73) * mm, "end": v(32, -15.17) * mm, "construction": true});
            skLineSegment(sketch, "E174", {"start": v(31, -14.54) * mm, "end": v(31.89, -16.36) * mm, "construction": true});
            skPoint(sketch, "E175", {"position": v(31.44, -15.45) * mm});
            skLineSegment(sketch, "E176", {"start": v(8.64, 16.04) * mm, "end": v(9.12, 15.83) * mm});
            skLineSegment(sketch, "E177", {"start": v(0.9, 15.73) * mm, "end": v(0.7, 17.35) * mm});
            skLineSegment(sketch, "E178", {"start": v(0.7, 17.35) * mm, "end": v(0.8, 17.35) * mm});
            skLineSegment(sketch, "E179", {"start": v(0.2, 16.26) * mm, "end": v(0.15, 16.21) * mm});
            skLineSegment(sketch, "E180", {"start": v(0.15, 16.21) * mm, "end": v(0.7, 15.42) * mm});
            skCircle(sketch, "E181", {"center": v(2.03, -1.53) * mm, "radius": 0.5 * mm});
            skText(sketch, "E182", { "text": "TESLA\ntesla", "fontName": "AllertaStencil-Regular.ttf"});
            skCircle(sketch, "E183", {"center": v(-29.59, 16) * mm, "radius": 0.5 * mm});
            skCircle(sketch, "E184", {"center": v(-30.85, 10.4) * mm, "radius": 0.42 * mm});
            skCircle(sketch, "E185", {"center": v(-31.06, 2.12) * mm, "radius": 0.71 * mm});
            skCircle(sketch, "E186", {"center": v(-36.35, 12.75) * mm, "radius": 0.77 * mm});
            skCircle(sketch, "E187", {"center": v(-25.96, 10.88) * mm, "radius": 0.63 * mm});
            skCircle(sketch, "E188.1.0.0", {"center": v(-31.94, 16.2) * mm, "radius": 0.77 * mm});
            skCircle(sketch, "E188.1.0.1", {"center": v(-26.44, 13.84) * mm, "radius": 0.42 * mm});
            skCircle(sketch, "E188.1.0.2", {"center": v(-21.54, 14.33) * mm, "radius": 0.63 * mm});
            skCircle(sketch, "E188.1.0.3", {"center": v(-25.17, 19.46) * mm, "radius": 0.5 * mm});
            skCircle(sketch, "E188.1.0.4", {"center": v(-26.65, 5.58) * mm, "radius": 0.71 * mm});
            skCircle(sketch, "E188.2.0.0", {"center": v(-27.52, 19.65) * mm, "radius": 0.77 * mm});
            skCircle(sketch, "E188.2.0.1", {"center": v(-22.03, 17.3) * mm, "radius": 0.42 * mm});
            skCircle(sketch, "E188.2.0.2", {"center": v(-17.13, 17.78) * mm, "radius": 0.63 * mm});
            skCircle(sketch, "E188.2.0.3", {"center": v(-20.76, 22.91) * mm, "radius": 0.5 * mm});
            skCircle(sketch, "E188.2.0.4", {"center": v(-22.23, 9.03) * mm, "radius": 0.71 * mm});
            skCircle(sketch, "E188.3.0.0", {"center": v(-23.11, 23.1) * mm, "radius": 0.77 * mm});
            skCircle(sketch, "E188.3.0.1", {"center": v(-17.62, 20.75) * mm, "radius": 0.42 * mm});
            skCircle(sketch, "E188.3.0.2", {"center": v(-12.72, 21.23) * mm, "radius": 0.63 * mm});
            skCircle(sketch, "E188.3.0.3", {"center": v(-16.35, 26.36) * mm, "radius": 0.5 * mm});
            skCircle(sketch, "E188.3.0.4", {"center": v(-17.82, 12.48) * mm, "radius": 0.71 * mm});
            skCircle(sketch, "E188.4.0.0", {"center": v(-18.7, 26.56) * mm, "radius": 0.77 * mm});
            skCircle(sketch, "E188.4.0.1", {"center": v(-13.2, 24.2) * mm, "radius": 0.42 * mm});
            skCircle(sketch, "E188.4.0.2", {"center": v(-8.3, 24.68) * mm, "radius": 0.63 * mm});
            skCircle(sketch, "E188.4.0.3", {"center": v(-11.94, 29.81) * mm, "radius": 0.5 * mm});
            skCircle(sketch, "E188.4.0.4", {"center": v(-13.41, 15.93) * mm, "radius": 0.71 * mm});
            skCircle(sketch, "E188.5.0.0", {"center": v(-14.29, 30) * mm, "radius": 0.77 * mm});
            skCircle(sketch, "E188.5.0.1", {"center": v(-8.8, 27.65) * mm, "radius": 0.42 * mm});
            skCircle(sketch, "E188.5.0.2", {"center": v(-3.9, 28.14) * mm, "radius": 0.63 * mm});
            skCircle(sketch, "E188.5.0.3", {"center": v(-7.52, 33.27) * mm, "radius": 0.5 * mm});
            skCircle(sketch, "E188.5.0.4", {"center": v(-9, 19.38) * mm, "radius": 0.71 * mm});
            skLineSegment(sketch, "E188.direction1", {"start": v(-36.35, 12.75) * mm, "end": v(-31.94, 16.2) * mm, "construction": true});
            const initialGuessF16  = {"E182": [-0.01476, -0.02046, 1, 0, 0.00635]};
            skSetInitialGuess(sketch, initialGuessF16);
            skSolve(sketch);
        }
        {
            var Q0;
            Q0 = qSketchRegion(id + "F16", true);
            extrude(context, id + "F17", {"entities" : qUnion([Q0]), "operationType" : NewBodyOperationType.REMOVE, "endBound" : BoundingType.UP_TO_NEXT, "oppositeDirection" : true, "depth" : 25.4 * mm});
        }
        {
            var Q0;
            Q0=sQuery(id+"F3.wireOp",BODY,"E1.0");
            deleteBodies(context, id + "F18", {"entities" : qUnion([Q0])});
        }
        {
            var Q0;
            Q0=makeQuery(id+"F13.opLoft","SWEPT_FACE",FACE,{"disambiguationData":[OSD([sQuery(id+"F11.wireOp",EDGE,"E9.1"),sQuery(id+"F11.wireOp",EDGE,"E9.2"),sQuery(id+"F11.wireOp",EDGE,"E9.3"),sQuery(id+"F12.wireOp",EDGE,"E10.1"),sQuery(id+"F12.wireOp",EDGE,"E10.2"),sQuery(id+"F12.wireOp",EDGE,"E10.3")])]});
            var sketch = newSketch(context, id + "F19", { "sketchPlane" : qUnion([Q0])});
            skCircle(sketch, "E189", {"center": v(-2.96, 43.01) * mm, "radius": 0.69 * mm});
            skCircle(sketch, "E190", {"center": v(-4.2, 44.12) * mm, "radius": 0.35 * mm});
            skCircle(sketch, "E191", {"center": v(-4.75, 42.44) * mm, "radius": 0.24 * mm});
            skCircle(sketch, "E192", {"center": v(-4.24, 43.05) * mm, "radius": 0.3 * mm});
            skCircle(sketch, "E193", {"center": v(-5.95, 43.84) * mm, "radius": 0.38 * mm});
            skCircle(sketch, "E194", {"center": v(-5.19, 43.26) * mm, "radius": 0.25 * mm});
            skCircle(sketch, "E195", {"center": v(-1.7, 44.23) * mm, "radius": 0.22 * mm});
            skCircle(sketch, "E196", {"center": v(0, 43.72) * mm, "radius": 0.3 * mm});
            skCircle(sketch, "E197", {"center": v(-1.04, 43.04) * mm, "radius": 0.44 * mm});
            skCircle(sketch, "E198", {"center": v(-1.87, 42.65) * mm, "radius": 0.24 * mm});
            skCircle(sketch, "E199", {"center": v(0.6, 42.39) * mm, "radius": 0.47 * mm});
            skCircle(sketch, "E200", {"center": v(1.3, 43.7) * mm, "radius": 0.4 * mm});
            skCircle(sketch, "E201", {"center": v(0.5, 44.57) * mm, "radius": 0.2 * mm});
            skCircle(sketch, "E202", {"center": v(-2.04, 41.83) * mm, "radius": 0.2 * mm});
            skCircle(sketch, "E203", {"center": v(-2.04, 40.93) * mm, "radius": 0.48 * mm});
            skCircle(sketch, "E204", {"center": v(-1.97, 40.04) * mm, "radius": 0.24 * mm});
            skCircle(sketch, "E205", {"center": v(-0.63, 39.15) * mm, "radius": 0.41 * mm});
            skCircle(sketch, "E206", {"center": v(-0.84, 40.31) * mm, "radius": 0.26 * mm});
            skCircle(sketch, "E207", {"center": v(-2.14, 38.9) * mm, "radius": 0.31 * mm});
            skCircle(sketch, "E208", {"center": v(-2.52, 36.88) * mm, "radius": 0.3 * mm});
            skCircle(sketch, "E209", {"center": v(-7.83, 43.6) * mm, "radius": 0.3 * mm});
            skCircle(sketch, "E210", {"center": v(-6.26, 42.75) * mm, "radius": 0.22 * mm});
            skCircle(sketch, "E211", {"center": v(-7.6, 42.27) * mm, "radius": 0.35 * mm});
            skCircle(sketch, "E212", {"center": v(-7.08, 43.16) * mm, "radius": 0.3 * mm});
            skCircle(sketch, "E213", {"center": v(3.17, 42.92) * mm, "radius": 0.5 * mm});
            skCircle(sketch, "E214", {"center": v(2.31, 42.06) * mm, "radius": 0.34 * mm});
            skCircle(sketch, "E215", {"center": v(2.45, 44.22) * mm, "radius": 0.24 * mm});
            skCircle(sketch, "E216", {"center": v(4.64, 44.08) * mm, "radius": 0.32 * mm});
            skCircle(sketch, "E217", {"center": v(4.92, 42.64) * mm, "radius": 0.24 * mm});
            skCircle(sketch, "E218", {"center": v(5.91, 43.4) * mm, "radius": 0.22 * mm});
            skCircle(sketch, "E219", {"center": v(-1.05, 41.75) * mm, "radius": 0.17 * mm});
            skCircle(sketch, "E220", {"center": v(0.67, 40.69) * mm, "radius": 0.38 * mm});
            skCircle(sketch, "E221", {"center": v(5.7, 44.4) * mm, "radius": 0.35 * mm});
            skCircle(sketch, "E222", {"center": v(6.12, 42) * mm, "radius": 0.4 * mm});
            skCircle(sketch, "E223", {"center": v(0.53, 39.11) * mm, "radius": 0.52 * mm});
            skCircle(sketch, "E224", {"center": v(0.7, 36.44) * mm, "radius": 0.24 * mm});
            skCircle(sketch, "E225", {"center": v(-0.57, 37.23) * mm, "radius": 0.34 * mm});
            skCircle(sketch, "E226", {"center": v(-0.8, 33.97) * mm, "radius": 0.27 * mm});
            skCircle(sketch, "E227", {"center": v(-1.97, 34.52) * mm, "radius": 0.32 * mm});
            skCircle(sketch, "E228", {"center": v(-1.97, 31.16) * mm, "radius": 0.2 * mm});
            skCircle(sketch, "E229", {"center": v(-0.3, 29.38) * mm, "radius": 0.38 * mm});
            skCircle(sketch, "E230", {"center": v(0.22, 32.4) * mm, "radius": 0.34 * mm});
            skCircle(sketch, "E231", {"center": v(0.87, 34.07) * mm, "radius": 0.41 * mm});
            skCircle(sketch, "E232", {"center": v(-0.4, 35.75) * mm, "radius": 0.48 * mm});
            skCircle(sketch, "E233", {"center": v(-2.04, 29.24) * mm, "radius": 0.38 * mm});
            skCircle(sketch, "E234", {"center": v(-7.73, 45.45) * mm, "radius": 0.4 * mm});
            skCircle(sketch, "E235", {"center": v(-8.17, 44.46) * mm, "radius": 0.2 * mm});
            skCircle(sketch, "E236", {"center": v(-8.24, 41.51) * mm, "radius": 0.2 * mm});
            skCircle(sketch, "E237", {"center": v(6.63, 44.9) * mm, "radius": 0.35 * mm});
            skCircle(sketch, "E238", {"center": v(1.56, 30.27) * mm, "radius": 0.33 * mm});
            skCircle(sketch, "E239", {"center": v(-0.43, 30.54) * mm, "radius": 0.42 * mm});
            skCircle(sketch, "E240", {"center": v(-1.39, 32.53) * mm, "radius": 0.4 * mm});
            skCircle(sketch, "E241", {"center": v(1.17, 28.5) * mm, "radius": 0.35 * mm});
            skCircle(sketch, "E242", {"center": v(3.86, 44.88) * mm, "radius": 0.29 * mm});
            skCircle(sketch, "E243", {"center": v(5.08, 45.21) * mm, "radius": 0.53 * mm});
            skCircle(sketch, "E244", {"center": v(-2.7, 45.25) * mm, "radius": 0.26 * mm});
            skCircle(sketch, "E245", {"center": v(-5.23, 45.41) * mm, "radius": 0.39 * mm});
            skCircle(sketch, "E246", {"center": v(1.94, 45.45) * mm, "radius": 0.4 * mm});
            skCircle(sketch, "E247", {"center": v(7.13, 33.96) * mm, "radius": 0.5 * mm});
            skCircle(sketch, "E248", {"center": v(8.9, 34.12) * mm, "radius": 0.29 * mm});
            skCircle(sketch, "E249", {"center": v(10.23, 33.95) * mm, "radius": 0.42 * mm});
            skCircle(sketch, "E250", {"center": v(8.02, 34.73) * mm, "radius": 0.2 * mm});
            skCircle(sketch, "E251", {"center": v(11.09, 34.52) * mm, "radius": 0.2 * mm});
            skCircle(sketch, "E252", {"center": v(11.18, 33.92) * mm, "radius": 0.21 * mm});
            skCircle(sketch, "E253", {"center": v(11.4, 35.98) * mm, "radius": 0.43 * mm});
            skCircle(sketch, "E254", {"center": v(10.2, 36.74) * mm, "radius": 0.32 * mm});
            skCircle(sketch, "E255", {"center": v(9.29, 36.98) * mm, "radius": 0.23 * mm});
            skCircle(sketch, "E256", {"center": v(9.8, 37.62) * mm, "radius": 0.33 * mm});
            skCircle(sketch, "E257", {"center": v(8.1, 37.68) * mm, "radius": 0.3 * mm});
            skCircle(sketch, "E258", {"center": v(7.06, 37.17) * mm, "radius": 0.33 * mm});
            skCircle(sketch, "E259", {"center": v(6.63, 36.16) * mm, "radius": 0.36 * mm});
            skCircle(sketch, "E260", {"center": v(6.68, 35.27) * mm, "radius": 0.38 * mm});
            skCircle(sketch, "E261", {"center": v(6.46, 32.8) * mm, "radius": 0.27 * mm});
            skCircle(sketch, "E262", {"center": v(6.24, 31.37) * mm, "radius": 0.54 * mm});
            skCircle(sketch, "E263", {"center": v(7.56, 30.87) * mm, "radius": 0.4 * mm});
            skCircle(sketch, "E264", {"center": v(9, 30.63) * mm, "radius": 0.5 * mm});
            skCircle(sketch, "E265", {"center": v(8.12, 29.96) * mm, "radius": 0.36 * mm});
            skCircle(sketch, "E266", {"center": v(10.3, 30.48) * mm, "radius": 0.26 * mm});
            skCircle(sketch, "E267", {"center": v(11.2, 30.44) * mm, "radius": 0.3 * mm});
            skCircle(sketch, "E268", {"center": v(7.1, 29.73) * mm, "radius": 0.24 * mm});
            skCircle(sketch, "E269", {"center": v(9.87, 29.56) * mm, "radius": 0.48 * mm});
            skCircle(sketch, "E270", {"center": v(9.49, 34.69) * mm, "radius": 0.33 * mm});
            skCircle(sketch, "E271", {"center": v(10.84, 37.29) * mm, "radius": 0.32 * mm});
            skCircle(sketch, "E272", {"center": v(8.85, 38.04) * mm, "radius": 0.23 * mm});
            skCircle(sketch, "E273", {"center": v(6.15, 34.5) * mm, "radius": 0.27 * mm});
            skCircle(sketch, "E274", {"center": v(5.97, 33.65) * mm, "radius": 0.3 * mm});
            skCircle(sketch, "E275", {"center": v(12.27, 34.17) * mm, "radius": 0.37 * mm});
            skCircle(sketch, "E276", {"center": v(12, 35.11) * mm, "radius": 0.37 * mm});
            skCircle(sketch, "E277", {"center": v(11.74, 37.05) * mm, "radius": 0.3 * mm});
            skCircle(sketch, "E278", {"center": v(11, 29.72) * mm, "radius": 0.2 * mm});
            skCircle(sketch, "E279", {"center": v(11.77, 31.49) * mm, "radius": 0.35 * mm});
            skCircle(sketch, "E280", {"center": v(12.5, 30.63) * mm, "radius": 0.32 * mm});
            skCircle(sketch, "E281", {"center": v(-10.91, 32.53) * mm, "radius": 0.56 * mm});
            skCircle(sketch, "E282", {"center": v(-12.24, 38.45) * mm, "radius": 0.27 * mm});
            skCircle(sketch, "E283", {"center": v(-7.51, 38.07) * mm, "radius": 0.5 * mm});
            skCircle(sketch, "E284", {"center": v(-5.68, 31.99) * mm, "radius": 0.48 * mm});
            skCircle(sketch, "E285", {"center": v(-13.84, 46.2) * mm, "radius": 0.61 * mm});
            skCircle(sketch, "E286", {"center": v(-5.42, 48.6) * mm, "radius": 0.27 * mm});
            skCircle(sketch, "E287", {"center": v(0.67, 47.83) * mm, "radius": 0.42 * mm});
            skCircle(sketch, "E288", {"center": v(7.44, 48.59) * mm, "radius": 0.58 * mm});
            skCircle(sketch, "E289", {"center": v(11.13, 44.38) * mm, "radius": 0.92 * mm});
            skCircle(sketch, "E290", {"center": v(13.47, 47.15) * mm, "radius": 0.29 * mm});
            skCircle(sketch, "E291", {"center": v(5, 27.37) * mm, "radius": 0.49 * mm});
            skCircle(sketch, "E292", {"center": v(10.93, 27.65) * mm, "radius": 0.46 * mm});
            skCircle(sketch, "E293", {"center": v(-9.97, 28.2) * mm, "radius": 0.55 * mm});
            skSolve(sketch);
        }
        {
            var Q0;
            Q0 = qSketchRegion(id + "F19", true);
            extrude(context, id + "F20", {"entities" : qUnion([Q0]), "operationType" : NewBodyOperationType.REMOVE, "oppositeDirection" : true, "depth" : 5.08 * mm});
        }
        {
            var Q0;
            Q0=makeQuery(id+"F13.opLoft","SWEPT_FACE",FACE,{"disambiguationData":[OSD([sQuery(id+"F11.wireOp",EDGE,"E9.0"),sQuery(id+"F11.wireOp",EDGE,"E9.1"),sQuery(id+"F11.wireOp",EDGE,"E9.2"),sQuery(id+"F12.wireOp",EDGE,"E10.0"),sQuery(id+"F12.wireOp",EDGE,"E10.1"),sQuery(id+"F12.wireOp",EDGE,"E10.2")])]});
            var sketch = newSketch(context, id + "F21", { "sketchPlane" : qUnion([Q0])});
            skCircle(sketch, "E294", {"center": v(-9.43, 37.33) * mm, "radius": 0.6 * mm});
            skCircle(sketch, "E295", {"center": v(-5.45, 38.54) * mm, "radius": 0.86 * mm});
            skCircle(sketch, "E296", {"center": v(-0.1, 42.14) * mm, "radius": 0.37 * mm});
            skCircle(sketch, "E297", {"center": v(2.6, 46.7) * mm, "radius": 0.75 * mm});
            skCircle(sketch, "E298", {"center": v(6.15, 34.78) * mm, "radius": 0.37 * mm});
            skCircle(sketch, "E299", {"center": v(-5.76, 30.72) * mm, "radius": 0.38 * mm});
            skCircle(sketch, "E300", {"center": v(-7.93, 46.37) * mm, "radius": 0.66 * mm});
            skCircle(sketch, "E301", {"center": v(13.31, 49.3) * mm, "radius": 0.38 * mm});
            skCircle(sketch, "E302", {"center": v(-8.05, 38.2) * mm, "radius": 0.25 * mm});
            skCircle(sketch, "E303", {"center": v(-6.87, 38.2) * mm, "radius": 0.28 * mm});
            skCircle(sketch, "E304", {"center": v(-5.8, 37.14) * mm, "radius": 0.33 * mm});
            skCircle(sketch, "E305", {"center": v(-9.43, 35.88) * mm, "radius": 0.48 * mm});
            skCircle(sketch, "E306", {"center": v(-9.07, 38.65) * mm, "radius": 0.33 * mm});
            skCircle(sketch, "E307", {"center": v(-8.16, 34.88) * mm, "radius": 0.37 * mm});
            skCircle(sketch, "E308", {"center": v(-6.2, 34.53) * mm, "radius": 0.5 * mm});
            skCircle(sketch, "E309", {"center": v(-5.66, 33.3) * mm, "radius": 0.28 * mm});
            skCircle(sketch, "E310", {"center": v(-6.24, 32.3) * mm, "radius": 0.38 * mm});
            skCircle(sketch, "E311", {"center": v(-6.92, 30.93) * mm, "radius": 0.46 * mm});
            skCircle(sketch, "E312", {"center": v(-8.8, 30.97) * mm, "radius": 0.31 * mm});
            skCircle(sketch, "E313", {"center": v(-10.8, 32.4) * mm, "radius": 0.42 * mm});
            skCircle(sketch, "E314", {"center": v(-10, 30.73) * mm, "radius": 0.69 * mm});
            skCircle(sketch, "E315", {"center": v(-4.76, 31.07) * mm, "radius": 0.4 * mm});
            skCircle(sketch, "E316", {"center": v(-5.07, 34.36) * mm, "radius": 0.46 * mm});
            skCircle(sketch, "E317", {"center": v(-7.6, 38.99) * mm, "radius": 0.17 * mm});
            skCircle(sketch, "E318", {"center": v(-7.88, 30.6) * mm, "radius": 0.34 * mm});
            skCircle(sketch, "E319", {"center": v(-4.66, 32.44) * mm, "radius": 0.62 * mm});
            skCircle(sketch, "E320", {"center": v(0, 41.25) * mm, "radius": 0.32 * mm});
            skCircle(sketch, "E321", {"center": v(1.03, 41.35) * mm, "radius": 0.34 * mm});
            skCircle(sketch, "E322", {"center": v(0.55, 39.81) * mm, "radius": 0.28 * mm});
            skCircle(sketch, "E323", {"center": v(-0.51, 38.4) * mm, "radius": 0.17 * mm});
            skCircle(sketch, "E324", {"center": v(0.68, 38.3) * mm, "radius": 0.25 * mm});
            skCircle(sketch, "E325", {"center": v(1.58, 35.53) * mm, "radius": 0.27 * mm});
            skCircle(sketch, "E326", {"center": v(0.79, 36) * mm, "radius": 0.24 * mm});
            skCircle(sketch, "E327", {"center": v(0.27, 37.1) * mm, "radius": 0.3 * mm});
            skCircle(sketch, "E328", {"center": v(0, 34.4) * mm, "radius": 0.4 * mm});
            skCircle(sketch, "E329", {"center": v(0.55, 32.03) * mm, "radius": 0.38 * mm});
            skCircle(sketch, "E330", {"center": v(1.1, 33.47) * mm, "radius": 0.31 * mm});
            skCircle(sketch, "E331", {"center": v(1.71, 30.93) * mm, "radius": 0.45 * mm});
            skCircle(sketch, "E332", {"center": v(1.99, 32.96) * mm, "radius": 0.43 * mm});
            skCircle(sketch, "E333", {"center": v(0, 30.8) * mm, "radius": 0.28 * mm});
            skCircle(sketch, "E334", {"center": v(0, 33.12) * mm, "radius": 0.3 * mm});
            skCircle(sketch, "E335", {"center": v(0, 35.94) * mm, "radius": 0.21 * mm});
            skCircle(sketch, "E336", {"center": v(-13.45, 45.22) * mm, "radius": 0.4 * mm});
            skCircle(sketch, "E337", {"center": v(6.55, 35.45) * mm, "radius": 0.28 * mm});
            skCircle(sketch, "E338", {"center": v(7.39, 35.75) * mm, "radius": 0.23 * mm});
            skCircle(sketch, "E339", {"center": v(6.99, 35.07) * mm, "radius": 0.1 * mm});
            skCircle(sketch, "E340", {"center": v(8.58, 35.64) * mm, "radius": 0.36 * mm});
            skCircle(sketch, "E341", {"center": v(9.63, 35.16) * mm, "radius": 0.27 * mm});
            skCircle(sketch, "E342", {"center": v(9.23, 33.46) * mm, "radius": 0.43 * mm});
            skCircle(sketch, "E343", {"center": v(9.66, 34.33) * mm, "radius": 0.25 * mm});
            skCircle(sketch, "E344", {"center": v(8.28, 33.13) * mm, "radius": 0.38 * mm});
            skCircle(sketch, "E345", {"center": v(7.67, 32.58) * mm, "radius": 0.27 * mm});
            skCircle(sketch, "E346", {"center": v(6.8, 32.49) * mm, "radius": 0.27 * mm});
            skCircle(sketch, "E347", {"center": v(6.44, 31.65) * mm, "radius": 0.21 * mm});
            skCircle(sketch, "E348", {"center": v(6.95, 30.38) * mm, "radius": 0.57 * mm});
            skCircle(sketch, "E349", {"center": v(8.37, 30.42) * mm, "radius": 0.34 * mm});
            skCircle(sketch, "E350", {"center": v(9.4, 30.52) * mm, "radius": 0.33 * mm});
            skCircle(sketch, "E351", {"center": v(9.63, 32.5) * mm, "radius": 0.4 * mm});
            skCircle(sketch, "E352", {"center": v(8.8, 32.68) * mm, "radius": 0.11 * mm});
            skCircle(sketch, "E353", {"center": v(9.95, 33.46) * mm, "radius": 0.2 * mm});
            skCircle(sketch, "E354", {"center": v(9.9, 31.7) * mm, "radius": 0.18 * mm});
            skCircle(sketch, "E355", {"center": v(10.08, 30.8) * mm, "radius": 0.15 * mm});
            skCircle(sketch, "E356", {"center": v(10.06, 29.85) * mm, "radius": 0.23 * mm});
            skCircle(sketch, "E357", {"center": v(7.05, 31.54) * mm, "radius": 0.2 * mm});
            skCircle(sketch, "E358", {"center": v(7.86, 35.2) * mm, "radius": 0.2 * mm});
            skCircle(sketch, "E359", {"center": v(9.74, 42.4) * mm, "radius": 0.24 * mm});
            skCircle(sketch, "E360", {"center": v(7.3, 49.04) * mm, "radius": 0.29 * mm});
            skCircle(sketch, "E361", {"center": v(-3.17, 27.51) * mm, "radius": 0.5 * mm});
            skCircle(sketch, "E362", {"center": v(-2.53, 45.6) * mm, "radius": 0.43 * mm});
            skCircle(sketch, "E363", {"center": v(-10.34, 41.86) * mm, "radius": 0.4 * mm});
            skCircle(sketch, "E364", {"center": v(-11.78, 49.08) * mm, "radius": 0.51 * mm});
            skCircle(sketch, "E365", {"center": v(-1.63, 49.58) * mm, "radius": 0.43 * mm});
            skCircle(sketch, "E366", {"center": v(14.16, 38.3) * mm, "radius": 0.81 * mm});
            skSolve(sketch);
        }
        {
            var Q0;
            Q0 = qSketchRegion(id + "F21", true);
            extrude(context, id + "F22", {"entities" : qUnion([Q0]), "operationType" : NewBodyOperationType.REMOVE, "endBound" : BoundingType.UP_TO_NEXT, "oppositeDirection" : true, "depth" : 25.4 * mm});
        }
        {
            var Q0;
            Q0=makeQuery(id+"F13.opLoft","SWEPT_FACE",FACE,{"disambiguationData":[OSD([sQuery(id+"F11.wireOp",EDGE,"E9.0"),sQuery(id+"F11.wireOp",EDGE,"E9.1"),sQuery(id+"F11.wireOp",EDGE,"E9.7"),sQuery(id+"F12.wireOp",EDGE,"E10.0"),sQuery(id+"F12.wireOp",EDGE,"E10.1"),sQuery(id+"F12.wireOp",EDGE,"E10.7")])]});
            var sketch = newSketch(context, id + "F23", { "sketchPlane" : qUnion([Q0])});
            skPoint(sketch, "E367", {"position": v(-16.2, 25.4) * mm});
            skCircle(sketch, "E368", {"center": v(0, 38.1) * mm, "radius": 5.72 * mm, "construction": true});
            skCircle(sketch, "E369", {"center": v(0, 38.1) * mm, "radius": 8.26 * mm, "construction": true});
            skCircle(sketch, "E370", {"center": v(0, 38.1) * mm, "radius": 2.54 * mm, "construction": true});
            skCircle(sketch, "E371", {"center": v(0, 38.1) * mm, "radius": 3.81 * mm, "construction": true});
            skCircle(sketch, "E372", {"center": v(0, 46.35) * mm, "radius": 0.5 * mm});
            skCircle(sketch, "E373", {"center": v(0, 43.81) * mm, "radius": 0.38 * mm});
            skCircle(sketch, "E374", {"center": v(0, 41.9) * mm, "radius": 0.25 * mm});
            skCircle(sketch, "E375", {"center": v(0, 40.64) * mm, "radius": 0.13 * mm});
            skCircle(sketch, "E376", {"center": v(0, 38.1) * mm, "radius": 10.8 * mm, "construction": true});
            skCircle(sketch, "E377", {"center": v(-1.42, 48.8) * mm, "radius": 0.64 * mm});
            skCircle(sketch, "E378.1.0", {"center": v(0.98, 48.85) * mm, "radius": 0.64 * mm});
            skCircle(sketch, "E378.1.1", {"center": v(1.83, 46.15) * mm, "radius": 0.5 * mm});
            skCircle(sketch, "E378.1.2", {"center": v(1.26, 43.67) * mm, "radius": 0.38 * mm});
            skCircle(sketch, "E378.1.3", {"center": v(0.84, 41.82) * mm, "radius": 0.25 * mm});
            skCircle(sketch, "E378.1.4", {"center": v(0.56, 40.58) * mm, "radius": 0.13 * mm});
            skCircle(sketch, "E378.2.0", {"center": v(3.33, 48.37) * mm, "radius": 0.64 * mm});
            skCircle(sketch, "E378.2.1", {"center": v(3.56, 45.55) * mm, "radius": 0.5 * mm});
            skCircle(sketch, "E378.2.2", {"center": v(2.47, 43.26) * mm, "radius": 0.38 * mm});
            skCircle(sketch, "E378.2.3", {"center": v(1.64, 41.54) * mm, "radius": 0.25 * mm});
            skCircle(sketch, "E378.2.4", {"center": v(1.1, 40.4) * mm, "radius": 0.13 * mm});
            skCircle(sketch, "E378.3.0", {"center": v(5.52, 47.38) * mm, "radius": 0.64 * mm});
            skCircle(sketch, "E378.3.1", {"center": v(5.12, 44.58) * mm, "radius": 0.5 * mm});
            skCircle(sketch, "E378.3.2", {"center": v(3.54, 42.58) * mm, "radius": 0.38 * mm});
            skCircle(sketch, "E378.3.3", {"center": v(2.36, 41.09) * mm, "radius": 0.25 * mm});
            skCircle(sketch, "E378.3.4", {"center": v(1.58, 40.1) * mm, "radius": 0.13 * mm});
            skCircle(sketch, "E378.4.0", {"center": v(7.44, 45.92) * mm, "radius": 0.64 * mm});
            skCircle(sketch, "E378.4.1", {"center": v(6.43, 43.28) * mm, "radius": 0.5 * mm});
            skCircle(sketch, "E378.4.2", {"center": v(4.45, 41.69) * mm, "radius": 0.38 * mm});
            skCircle(sketch, "E378.4.3", {"center": v(2.97, 40.5) * mm, "radius": 0.25 * mm});
            skCircle(sketch, "E378.4.4", {"center": v(1.98, 39.7) * mm, "radius": 0.13 * mm});
            skCircle(sketch, "E378.5.0", {"center": v(8.98, 44.09) * mm, "radius": 0.64 * mm});
            skCircle(sketch, "E378.5.1", {"center": v(7.41, 41.73) * mm, "radius": 0.5 * mm});
            skCircle(sketch, "E378.5.2", {"center": v(5.13, 40.62) * mm, "radius": 0.38 * mm});
            skCircle(sketch, "E378.5.3", {"center": v(3.42, 39.78) * mm, "radius": 0.25 * mm});
            skCircle(sketch, "E378.5.4", {"center": v(2.28, 39.22) * mm, "radius": 0.13 * mm});
            skCircle(sketch, "E378.6.0", {"center": v(10.08, 41.95) * mm, "radius": 0.64 * mm});
            skCircle(sketch, "E378.6.1", {"center": v(8.03, 40) * mm, "radius": 0.5 * mm});
            skCircle(sketch, "E378.6.2", {"center": v(5.56, 39.42) * mm, "radius": 0.38 * mm});
            skCircle(sketch, "E378.6.3", {"center": v(3.7, 38.98) * mm, "radius": 0.25 * mm});
            skCircle(sketch, "E378.6.4", {"center": v(2.47, 38.69) * mm, "radius": 0.13 * mm});
            skCircle(sketch, "E378.7.0", {"center": v(10.69, 39.63) * mm, "radius": 0.64 * mm});
            skCircle(sketch, "E378.7.1", {"center": v(8.25, 38.18) * mm, "radius": 0.5 * mm});
            skCircle(sketch, "E378.7.2", {"center": v(5.71, 38.16) * mm, "radius": 0.38 * mm});
            skCircle(sketch, "E378.7.3", {"center": v(3.8, 38.14) * mm, "radius": 0.25 * mm});
            skCircle(sketch, "E378.7.4", {"center": v(2.54, 38.12) * mm, "radius": 0.13 * mm});
            skCircle(sketch, "E378.8.0", {"center": v(10.76, 37.22) * mm, "radius": 0.64 * mm});
            skCircle(sketch, "E378.8.1", {"center": v(8.07, 36.35) * mm, "radius": 0.5 * mm});
            skCircle(sketch, "E378.8.2", {"center": v(5.59, 36.9) * mm, "radius": 0.38 * mm});
            skCircle(sketch, "E378.8.3", {"center": v(3.72, 37.3) * mm, "radius": 0.25 * mm});
            skCircle(sketch, "E378.8.4", {"center": v(2.48, 37.56) * mm, "radius": 0.13 * mm});
            skCircle(sketch, "E378.9.0", {"center": v(10.3, 34.87) * mm, "radius": 0.64 * mm});
            skCircle(sketch, "E378.9.1", {"center": v(7.48, 34.61) * mm, "radius": 0.5 * mm});
            skCircle(sketch, "E378.9.2", {"center": v(5.18, 35.68) * mm, "radius": 0.38 * mm});
            skCircle(sketch, "E378.9.3", {"center": v(3.45, 36.49) * mm, "radius": 0.25 * mm});
            skCircle(sketch, "E378.9.4", {"center": v(2.3, 37.03) * mm, "radius": 0.13 * mm});
            skCircle(sketch, "E378.10.0", {"center": v(9.33, 32.67) * mm, "radius": 0.64 * mm});
            skCircle(sketch, "E378.10.1", {"center": v(6.52, 33.04) * mm, "radius": 0.5 * mm});
            skCircle(sketch, "E378.10.2", {"center": v(4.52, 34.6) * mm, "radius": 0.38 * mm});
            skCircle(sketch, "E378.10.3", {"center": v(3.01, 35.77) * mm, "radius": 0.25 * mm});
            skCircle(sketch, "E378.10.4", {"center": v(2, 36.54) * mm, "radius": 0.13 * mm});
            skCircle(sketch, "E378.11.0", {"center": v(7.9, 30.74) * mm, "radius": 0.64 * mm});
            skCircle(sketch, "E378.11.1", {"center": v(5.24, 31.73) * mm, "radius": 0.5 * mm});
            skCircle(sketch, "E378.11.2", {"center": v(3.63, 33.69) * mm, "radius": 0.38 * mm});
            skCircle(sketch, "E378.11.3", {"center": v(2.42, 35.16) * mm, "radius": 0.25 * mm});
            skCircle(sketch, "E378.11.4", {"center": v(1.61, 36.14) * mm, "radius": 0.13 * mm});
            skCircle(sketch, "E378.12.0", {"center": v(6.07, 29.18) * mm, "radius": 0.64 * mm});
            skCircle(sketch, "E378.12.1", {"center": v(3.7, 30.72) * mm, "radius": 0.5 * mm});
            skCircle(sketch, "E378.12.2", {"center": v(2.56, 33) * mm, "radius": 0.38 * mm});
            skCircle(sketch, "E378.12.3", {"center": v(1.7, 34.7) * mm, "radius": 0.25 * mm});
            skCircle(sketch, "E378.12.4", {"center": v(1.14, 35.83) * mm, "radius": 0.13 * mm});
            skCircle(sketch, "E378.13.0", {"center": v(3.95, 28.05) * mm, "radius": 0.64 * mm});
            skCircle(sketch, "E378.13.1", {"center": v(1.98, 30.09) * mm, "radius": 0.5 * mm});
            skCircle(sketch, "E378.13.2", {"center": v(1.37, 32.55) * mm, "radius": 0.38 * mm});
            skCircle(sketch, "E378.13.3", {"center": v(0.91, 34.4) * mm, "radius": 0.25 * mm});
            skCircle(sketch, "E378.13.4", {"center": v(0.6, 35.63) * mm, "radius": 0.13 * mm});
            skCircle(sketch, "E378.14.0", {"center": v(1.63, 27.43) * mm, "radius": 0.64 * mm});
            skCircle(sketch, "E378.14.1", {"center": v(0.16, 29.85) * mm, "radius": 0.5 * mm});
            skCircle(sketch, "E378.14.2", {"center": v(0.11, 32.39) * mm, "radius": 0.38 * mm});
            skCircle(sketch, "E378.14.3", {"center": v(0.07, 34.3) * mm, "radius": 0.25 * mm});
            skCircle(sketch, "E378.14.4", {"center": v(0.05, 35.56) * mm, "radius": 0.13 * mm});
            skCircle(sketch, "E378.15.0", {"center": v(-0.77, 27.33) * mm, "radius": 0.64 * mm});
            skCircle(sketch, "E378.15.1", {"center": v(-1.67, 30.02) * mm, "radius": 0.5 * mm});
            skCircle(sketch, "E378.15.2", {"center": v(-1.16, 32.5) * mm, "radius": 0.38 * mm});
            skCircle(sketch, "E378.15.3", {"center": v(-0.77, 34.37) * mm, "radius": 0.25 * mm});
            skCircle(sketch, "E378.15.4", {"center": v(-0.51, 35.61) * mm, "radius": 0.13 * mm});
            skCircle(sketch, "E378.16.0", {"center": v(-3.13, 27.77) * mm, "radius": 0.64 * mm});
            skCircle(sketch, "E378.16.1", {"center": v(-3.42, 30.58) * mm, "radius": 0.5 * mm});
            skCircle(sketch, "E378.16.2", {"center": v(-2.36, 32.9) * mm, "radius": 0.38 * mm});
            skCircle(sketch, "E378.16.3", {"center": v(-1.58, 34.63) * mm, "radius": 0.25 * mm});
            skCircle(sketch, "E378.16.4", {"center": v(-1.05, 35.79) * mm, "radius": 0.13 * mm});
            skCircle(sketch, "E378.17.0", {"center": v(-5.34, 28.72) * mm, "radius": 0.64 * mm});
            skCircle(sketch, "E378.17.1", {"center": v(-5, 31.53) * mm, "radius": 0.5 * mm});
            skCircle(sketch, "E378.17.2", {"center": v(-3.46, 33.55) * mm, "radius": 0.38 * mm});
            skCircle(sketch, "E378.17.3", {"center": v(-2.3, 35.07) * mm, "radius": 0.25 * mm});
            skCircle(sketch, "E378.17.4", {"center": v(-1.54, 36.08) * mm, "radius": 0.13 * mm});
            skCircle(sketch, "E378.18.0", {"center": v(-7.28, 30.13) * mm, "radius": 0.64 * mm});
            skCircle(sketch, "E378.18.1", {"center": v(-6.32, 32.8) * mm, "radius": 0.5 * mm});
            skCircle(sketch, "E378.18.2", {"center": v(-4.38, 34.43) * mm, "radius": 0.38 * mm});
            skCircle(sketch, "E378.18.3", {"center": v(-2.92, 35.65) * mm, "radius": 0.25 * mm});
            skCircle(sketch, "E378.18.4", {"center": v(-1.95, 36.47) * mm, "radius": 0.13 * mm});
            skCircle(sketch, "E378.19.0", {"center": v(-8.87, 31.94) * mm, "radius": 0.64 * mm});
            skCircle(sketch, "E378.19.1", {"center": v(-7.34, 34.32) * mm, "radius": 0.5 * mm});
            skCircle(sketch, "E378.19.2", {"center": v(-5.08, 35.49) * mm, "radius": 0.38 * mm});
            skCircle(sketch, "E378.19.3", {"center": v(-3.39, 36.36) * mm, "radius": 0.25 * mm});
            skCircle(sketch, "E378.19.4", {"center": v(-2.26, 36.94) * mm, "radius": 0.13 * mm});
            skCircle(sketch, "E378.20.0", {"center": v(-10, 34.05) * mm, "radius": 0.64 * mm});
            skCircle(sketch, "E378.20.1", {"center": v(-8, 36.04) * mm, "radius": 0.5 * mm});
            skCircle(sketch, "E378.20.2", {"center": v(-5.53, 36.67) * mm, "radius": 0.38 * mm});
            skCircle(sketch, "E378.20.3", {"center": v(-3.69, 37.15) * mm, "radius": 0.25 * mm});
            skCircle(sketch, "E378.20.4", {"center": v(-2.46, 37.47) * mm, "radius": 0.13 * mm});
            skCircle(sketch, "E378.21.0", {"center": v(-10.66, 36.37) * mm, "radius": 0.64 * mm});
            skCircle(sketch, "E378.21.1", {"center": v(-8.25, 37.86) * mm, "radius": 0.5 * mm});
            skCircle(sketch, "E378.21.2", {"center": v(-5.71, 37.93) * mm, "radius": 0.38 * mm});
            skCircle(sketch, "E378.21.3", {"center": v(-3.8, 37.99) * mm, "radius": 0.25 * mm});
            skCircle(sketch, "E378.21.4", {"center": v(-2.54, 38.03) * mm, "radius": 0.13 * mm});
            skCircle(sketch, "E378.22.0", {"center": v(-10.77, 38.77) * mm, "radius": 0.64 * mm});
            skCircle(sketch, "E378.22.1", {"center": v(-8.1, 39.7) * mm, "radius": 0.5 * mm});
            skCircle(sketch, "E378.22.2", {"center": v(-5.6, 39.2) * mm, "radius": 0.38 * mm});
            skCircle(sketch, "E378.22.3", {"center": v(-3.74, 38.83) * mm, "radius": 0.25 * mm});
            skCircle(sketch, "E378.22.4", {"center": v(-2.5, 38.59) * mm, "radius": 0.13 * mm});
            skCircle(sketch, "E378.23.0", {"center": v(-10.36, 41.13) * mm, "radius": 0.64 * mm});
            skCircle(sketch, "E378.23.1", {"center": v(-7.55, 41.44) * mm, "radius": 0.5 * mm});
            skCircle(sketch, "E378.23.2", {"center": v(-5.23, 40.41) * mm, "radius": 0.38 * mm});
            skCircle(sketch, "E378.23.3", {"center": v(-3.48, 39.64) * mm, "radius": 0.25 * mm});
            skCircle(sketch, "E378.23.4", {"center": v(-2.32, 39.13) * mm, "radius": 0.13 * mm});
            skCircle(sketch, "E378.24.0", {"center": v(-9.43, 43.35) * mm, "radius": 0.64 * mm});
            skCircle(sketch, "E378.24.1", {"center": v(-6.62, 43.03) * mm, "radius": 0.5 * mm});
            skCircle(sketch, "E378.24.2", {"center": v(-4.58, 41.51) * mm, "radius": 0.38 * mm});
            skCircle(sketch, "E378.24.3", {"center": v(-3.06, 40.38) * mm, "radius": 0.25 * mm});
            skCircle(sketch, "E378.24.4", {"center": v(-2.04, 39.62) * mm, "radius": 0.13 * mm});
            skCircle(sketch, "E378.25.0", {"center": v(-8.04, 45.3) * mm, "radius": 0.64 * mm});
            skCircle(sketch, "E378.25.1", {"center": v(-5.37, 44.37) * mm, "radius": 0.5 * mm});
            skCircle(sketch, "E378.25.2", {"center": v(-3.72, 42.44) * mm, "radius": 0.38 * mm});
            skCircle(sketch, "E378.25.3", {"center": v(-2.48, 41) * mm, "radius": 0.25 * mm});
            skCircle(sketch, "E378.25.4", {"center": v(-1.65, 40.03) * mm, "radius": 0.13 * mm});
            skCircle(sketch, "E378.26.0", {"center": v(-6.24, 46.9) * mm, "radius": 0.64 * mm});
            skCircle(sketch, "E378.26.1", {"center": v(-3.85, 45.4) * mm, "radius": 0.5 * mm});
            skCircle(sketch, "E378.26.2", {"center": v(-2.66, 43.16) * mm, "radius": 0.38 * mm});
            skCircle(sketch, "E378.26.3", {"center": v(-1.78, 41.47) * mm, "radius": 0.25 * mm});
            skCircle(sketch, "E378.26.4", {"center": v(-1.18, 40.35) * mm, "radius": 0.13 * mm});
            skCircle(sketch, "E378.27.0", {"center": v(-4.14, 48.07) * mm, "radius": 0.64 * mm});
            skCircle(sketch, "E378.27.1", {"center": v(-2.14, 46.07) * mm, "radius": 0.5 * mm});
            skCircle(sketch, "E378.27.2", {"center": v(-1.48, 43.62) * mm, "radius": 0.38 * mm});
            skCircle(sketch, "E378.27.3", {"center": v(-0.99, 41.78) * mm, "radius": 0.25 * mm});
            skCircle(sketch, "E378.27.4", {"center": v(-0.66, 40.55) * mm, "radius": 0.13 * mm});
            skLineSegment(sketch, "E378.anchor1", {"start": v(0, 38.1) * mm, "end": v(-1.42, 48.8) * mm, "construction": true});
            skLineSegment(sketch, "E378.anchor2", {"start": v(0, 38.1) * mm, "end": v(-4.14, 48.07) * mm, "construction": true});
            skSolve(sketch);
        }
        {
            var Q0;
            Q0 = qSketchRegion(id + "F23", true);
            extrude(context, id + "F24", {"entities" : qUnion([Q0]), "operationType" : NewBodyOperationType.REMOVE, "endBound" : BoundingType.UP_TO_NEXT, "oppositeDirection" : true, "depth" : 25.4 * mm});
        }
        {
            var Q0;
            Q0=makeQuery(id+"F13.opLoft","SWEPT_FACE",FACE,{"disambiguationData":[OSD([sQuery(id+"F11.wireOp",EDGE,"E9.0"),sQuery(id+"F11.wireOp",EDGE,"E9.6"),sQuery(id+"F11.wireOp",EDGE,"E9.7"),sQuery(id+"F12.wireOp",EDGE,"E10.0"),sQuery(id+"F12.wireOp",EDGE,"E10.6"),sQuery(id+"F12.wireOp",EDGE,"E10.7")])]});
            var sketch = newSketch(context, id + "F25", { "sketchPlane" : qUnion([Q0])});
            skPoint(sketch, "E379", {"position": v(-16.2, 25.4) * mm});
            skCircle(sketch, "E380", {"center": v(0, 38.1) * mm, "radius": 5.72 * mm, "construction": true});
            skCircle(sketch, "E381", {"center": v(0, 38.1) * mm, "radius": 8.26 * mm, "construction": true});
            skCircle(sketch, "E382", {"center": v(0, 38.1) * mm, "radius": 2.54 * mm, "construction": true});
            skCircle(sketch, "E383", {"center": v(0, 38.1) * mm, "radius": 3.81 * mm, "construction": true});
            skCircle(sketch, "E384", {"center": v(0.5, 46.34) * mm, "radius": 0.5 * mm});
            skCircle(sketch, "E385", {"center": v(1.02, 43.72) * mm, "radius": 0.38 * mm});
            skCircle(sketch, "E386", {"center": v(0.38, 41.9) * mm, "radius": 0.25 * mm});
            skCircle(sketch, "E387", {"center": v(0, 40.64) * mm, "radius": 0.13 * mm});
            skCircle(sketch, "E388", {"center": v(0, 38.1) * mm, "radius": 10.8 * mm, "construction": true});
            skCircle(sketch, "E389", {"center": v(0, 48.9) * mm, "radius": 0.64 * mm});
            skCircle(sketch, "E390.1.0", {"center": v(6.2, 46.94) * mm, "radius": 0.64 * mm});
            skCircle(sketch, "E390.1.1", {"center": v(5.14, 44.56) * mm, "radius": 0.5 * mm});
            skCircle(sketch, "E390.1.2", {"center": v(4.06, 42.12) * mm, "radius": 0.38 * mm});
            skCircle(sketch, "E390.1.3", {"center": v(2.49, 40.99) * mm, "radius": 0.25 * mm});
            skCircle(sketch, "E390.1.4", {"center": v(1.46, 40.18) * mm, "radius": 0.13 * mm});
            skCircle(sketch, "E390.2.0", {"center": v(10.14, 41.8) * mm, "radius": 0.64 * mm});
            skCircle(sketch, "E390.2.1", {"center": v(7.92, 40.44) * mm, "radius": 0.5 * mm});
            skCircle(sketch, "E390.2.2", {"center": v(5.63, 39.07) * mm, "radius": 0.38 * mm});
            skCircle(sketch, "E390.2.3", {"center": v(3.7, 39.04) * mm, "radius": 0.25 * mm});
            skCircle(sketch, "E390.2.4", {"center": v(2.39, 38.97) * mm, "radius": 0.13 * mm});
            skCircle(sketch, "E390.3.0", {"center": v(10.43, 35.3) * mm, "radius": 0.63 * mm});
            skCircle(sketch, "E390.3.1", {"center": v(7.83, 35.48) * mm, "radius": 0.5 * mm});
            skCircle(sketch, "E390.3.2", {"center": v(5.17, 35.66) * mm, "radius": 0.38 * mm});
            skCircle(sketch, "E390.3.3", {"center": v(3.56, 36.75) * mm, "radius": 0.25 * mm});
            skCircle(sketch, "E390.3.4", {"center": v(2.45, 37.44) * mm, "radius": 0.13 * mm});
            skCircle(sketch, "E390.4.0", {"center": v(6.94, 29.83) * mm, "radius": 0.64 * mm});
            skCircle(sketch, "E390.4.1", {"center": v(4.9, 31.46) * mm, "radius": 0.5 * mm});
            skCircle(sketch, "E390.4.2", {"center": v(2.84, 33.14) * mm, "radius": 0.38 * mm});
            skCircle(sketch, "E390.4.3", {"center": v(2.14, 34.95) * mm, "radius": 0.25 * mm});
            skCircle(sketch, "E390.4.4", {"center": v(1.63, 36.15) * mm, "radius": 0.13 * mm});
            skLineSegment(sketch, "E390.anchor1", {"start": v(0, 38.1) * mm, "end": v(0, 48.9) * mm, "construction": true});
            skLineSegment(sketch, "E390.anchor2", {"start": v(0, 38.1) * mm, "end": v(-7.63, 45.73) * mm, "construction": true});
            skCircle(sketch, "E391.1.5.0", {"center": v(0.94, 27.35) * mm, "radius": 0.64 * mm});
            skCircle(sketch, "E391.2.5.0", {"center": v(0.21, 29.85) * mm, "radius": 0.5 * mm});
            skCircle(sketch, "E391.4.5.0", {"center": v(-0.52, 32.4) * mm, "radius": 0.38 * mm});
            skCircle(sketch, "E391.6.5.0", {"center": v(-0.05, 34.3) * mm, "radius": 0.25 * mm});
            skCircle(sketch, "E391.8.5.0", {"center": v(0.22, 35.57) * mm, "radius": 0.13 * mm});
            skCircle(sketch, "E391.1.6.0", {"center": v(-5.4, 28.75) * mm, "radius": 0.64 * mm});
            skCircle(sketch, "E391.2.6.0", {"center": v(-4.56, 31.22) * mm, "radius": 0.5 * mm});
            skCircle(sketch, "E391.4.6.0", {"center": v(-3.7, 33.74) * mm, "radius": 0.38 * mm});
            skCircle(sketch, "E391.6.6.0", {"center": v(-2.23, 35) * mm, "radius": 0.25 * mm});
            skCircle(sketch, "E391.8.6.0", {"center": v(-1.27, 35.9) * mm, "radius": 0.13 * mm});
            skCircle(sketch, "E391.1.7.0", {"center": v(-9.78, 33.54) * mm, "radius": 0.64 * mm});
            skCircle(sketch, "E391.2.7.0", {"center": v(-7.68, 35.08) * mm, "radius": 0.5 * mm});
            skCircle(sketch, "E391.4.7.0", {"center": v(-5.53, 36.64) * mm, "radius": 0.38 * mm});
            skCircle(sketch, "E391.6.7.0", {"center": v(-3.6, 36.84) * mm, "radius": 0.25 * mm});
            skCircle(sketch, "E391.8.7.0", {"center": v(-2.3, 37.03) * mm, "radius": 0.13 * mm});
            skCircle(sketch, "E391.1.8.0", {"center": v(-10.63, 39.97) * mm, "radius": 0.64 * mm});
            skCircle(sketch, "E391.2.8.0", {"center": v(-8.03, 40.03) * mm, "radius": 0.5 * mm});
            skCircle(sketch, "E391.4.8.0", {"center": v(-5.36, 40.08) * mm, "radius": 0.38 * mm});
            skCircle(sketch, "E391.6.8.0", {"center": v(-3.67, 39.13) * mm, "radius": 0.25 * mm});
            skCircle(sketch, "E391.8.8.0", {"center": v(-2.5, 38.54) * mm, "radius": 0.13 * mm});
            skCircle(sketch, "E392.1.9.0", {"center": v(-7.63, 45.73) * mm, "radius": 0.64 * mm});
            skCircle(sketch, "E392.2.9.0", {"center": v(-5.47, 44.29) * mm, "radius": 0.5 * mm});
            skCircle(sketch, "E392.4.9.0", {"center": v(-3.26, 42.8) * mm, "radius": 0.38 * mm});
            skCircle(sketch, "E392.6.9.0", {"center": v(-2.41, 41.05) * mm, "radius": 0.25 * mm});
            skCircle(sketch, "E392.8.9.0", {"center": v(-1.8, 39.9) * mm, "radius": 0.13 * mm});
            skCircle(sketch, "E393.cCircle", {"center": v(0, 38.1) * mm, "radius": 0.69 * mm, "construction": true});
            skLineSegment(sketch, "E393.0", {"start": v(-1.33, 38.46) * mm, "end": v(0.98, 39.07) * mm});
            skLineSegment(sketch, "E393.1", {"start": v(0.98, 39.07) * mm, "end": v(0.35, 36.77) * mm});
            skLineSegment(sketch, "E393.2", {"start": v(0.35, 36.77) * mm, "end": v(-1.33, 38.46) * mm});
            skPoint(sketch, "E393.0.midPoint", {"position": v(-0.17, 38.77) * mm});
            skSolve(sketch);
        }
        {
            var Q0;
            Q0 = qSketchRegion(id + "F25", true);
            extrude(context, id + "F26", {"entities" : qUnion([Q0]), "operationType" : NewBodyOperationType.REMOVE, "endBound" : BoundingType.UP_TO_NEXT, "oppositeDirection" : true, "depth" : 25.4 * mm});
        }
        {
            var Q0;
            Q0=makeQuery(id+"F7.opLoft","SWEPT_FACE",FACE,{"disambiguationData":[OSD([sQuery(id+"F5.wireOp",EDGE,"E4.1"),sQuery(id+"F5.wireOp",EDGE,"E4.2"),sQuery(id+"F5.wireOp",EDGE,"E4.3"),sQuery(id+"F6.wireOp",EDGE,"E5.1"),sQuery(id+"F6.wireOp",EDGE,"E5.2"),sQuery(id+"F6.wireOp",EDGE,"E5.3")])]});
            var sketch = newSketch(context, id + "F27", { "sketchPlane" : qUnion([Q0])});
            skCircle(sketch, "E394", {"center": v(38.22, 0.3) * mm, "radius": 0.2 * mm});
            skCircle(sketch, "E395", {"center": v(38.64, 6.46) * mm, "radius": 0.42 * mm});
            skCircle(sketch, "E396", {"center": v(33.18, 4.41) * mm, "radius": 0.62 * mm});
            skCircle(sketch, "E397", {"center": v(35.9, -1.72) * mm, "radius": 0.4 * mm});
            skCircle(sketch, "E398", {"center": v(35.13, -5.47) * mm, "radius": 0.45 * mm});
            skCircle(sketch, "E399", {"center": v(39.23, -5.62) * mm, "radius": 0.57 * mm});
            skCircle(sketch, "E400", {"center": v(38.8, -2.27) * mm, "radius": 0.25 * mm});
            skCircle(sketch, "E401", {"center": v(31.03, 0) * mm, "radius": 0.3 * mm});
            skCircle(sketch, "E402", {"center": v(41.17, -9.15) * mm, "radius": 0.32 * mm});
            skCircle(sketch, "E403", {"center": v(43.17, -1.52) * mm, "radius": 0.28 * mm});
            skCircle(sketch, "E404", {"center": v(42.4, 7.96) * mm, "radius": 0.32 * mm});
            skCircle(sketch, "E405", {"center": v(36.15, 11.7) * mm, "radius": 0.3 * mm});
            skCircle(sketch, "E406", {"center": v(32.13, 7.27) * mm, "radius": 0.31 * mm});
            skCircle(sketch, "E407", {"center": v(40.61, 11.03) * mm, "radius": 0.2 * mm});
            skCircle(sketch, "E408", {"center": v(41.89, 2.68) * mm, "radius": 0.28 * mm});
            skCircle(sketch, "E409", {"center": v(44.29, -10.67) * mm, "radius": 0.49 * mm});
            skCircle(sketch, "E410", {"center": v(45.06, 9.84) * mm, "radius": 0.36 * mm});
            skCircle(sketch, "E411", {"center": v(38.96, 3.61) * mm, "radius": 0.3 * mm});
            skCircle(sketch, "E412", {"center": v(30.16, 4.02) * mm, "radius": 0.3 * mm});
            skCircle(sketch, "E413", {"center": v(30.7, -4.17) * mm, "radius": 0.49 * mm});
            skSolve(sketch);
        }
        {
            var Q0;
            Q0 = qSketchRegion(id + "F27", true);
            extrude(context, id + "F28", {"entities" : qUnion([Q0]), "operationType" : NewBodyOperationType.REMOVE, "endBound" : BoundingType.UP_TO_NEXT, "oppositeDirection" : true, "depth" : 25.4 * mm});
        }
    });
